FCSTD DOCUMENT  (FreeCAD 1.1R20260223 (Git shallow))
Label: wallspeakers prototype v5
License: All rights reserved
LicenseURL: http://en.wikipedia.org/wiki/All_rights_reserved
objects: TechDraw::DrawViewDimension×26, Sketcher::SketchObject×23, App::Point×12, PartDesign::Pad×11, PartDesign::Body×10, TechDraw::DrawViewAnnotation×10, PartDesign::Pocket×6, PartDesign::Hole×5, TechDraw::DrawSVGTemplate×5, TechDraw::DrawViewImage×5, TechDraw::DrawPage×5, App::DocumentObjectGroup×4, PartDesign::Revolution×3, TechDraw::DrawProjGroupItem×3, TechDraw::DrawViewDimExtent×3, PartDesign::Chamfer×3, PartDesign::Fillet×2, App::Part×2, Spreadsheet::Sheet×1, PartDesign::Thickness×1, +5 more types
note: 201 computed .brp shape members not serialized (recipe doc carries the construction recipe); baked Part::Feature solids carry a one-line shape summary decoded from their .brp

FEATURE [Spreadsheet::Sheet] Spreadsheet  label="dim"
  cells = A1='ext_width; B1(ext_width)=200; A2='ext_length; B2(ext_length)=500; A3='back_panel_width; B3(back_panel_width)==B1 - B13 * 2; C3='ext_width - rim_width * 2; A4='back_panel_length; B4(back_panel_length)==B2 - B13 * 2; C4='ext_length - rim_width * 2; A5='back_panel_radius; B5(back_panel_radius)==B11 - B13; C5='corner_roundover - rim_width; A6='back_thickness; B6(back_thickness)=5; A7='front_thickness; B7(front_thickness)=5; A8='total_depth; B8(total_depth)=48; C8='giving ourselves 2mm for wall mount fittings etc; A9='wall_thickness; B9(wall_thickness)=5; A10='front_roundover; B10(front_roundover)=10; A11='corner_roundover; B11(corner_roundover)=10; A13='rim_width; B13(rim_width)=3; A14='rim_depth; B14(rim_depth)=5.7; C14='allowing 0.7mm for a compressed 0.8mm gasket; A15='post_diameter; B15(post_diameter)=14; A17='bmr_x; B17(bmr_x)=45; C17='nudging a bit closer to the centre; A18='bmr_y; B18(bmr_y)=0; A19='bmr_screw_distance; B19(bmr_screw_distance)=24; A20='bmr_screw_offset; B20(bmr_screw_offset)=16.95; C20='bmr_screw_distance * sin(45); A21='bmr_hole_diameter; B21(bmr_hole_diameter)=41; A22='bmr_rebate_depth; B22(bmr_rebate_depth)=6; A23='bmr_post_width; B23(bmr_post_width)=7; A24='bmr_rebate_diameter; B24(bmr_rebate_diameter)=60; A26='woofer_x; B26(woofer_x)=0; A27='woofer_y; B27(woofer_y)=120; A28='woofer_support_thickness; B28(woofer_support_thickness)=7; C28='resulting in wall (5mm) + this (7mm) - rebate (8mm) = 5mm; A29='woofer_support_diameter; B29(woofer_support_diameter)=165; A30='woofer_screw_distance; B30(woofer_screw_thickness)=70.05; A31='woofer_screw_offset; B31(woofer_screw_offset)==B30 * 0.707; C31='woofer_screw_distance * sin(45); A32='woofer_hole_diameter; B32(woofer_hole_diameter)=130; A33='woofer_rebate_depth; B33(woofer_rebate_depth)=8; C33='5.3 for woofer rim, 0.7 for compressed gasket, 2 for cone resting excursion; A34='woofer_rebate_diameter; B34(woofer_rebate_diameter)=152.5; A39='woofer cutout spec; B39=127.5; C39=0.3; A40='woofer rebate spec; B40=152; C40=0.3; A41='woofer rebate depth spec; B41=5.3; C41=0.3; A43='gasket thickness (compressed); B43=0.7
FEATURE [Sketcher::SketchObject] Sketch  label="outline"
  ArcFitTolerance = 1e-06
  AttachmentSupport = -> [XY_Plane]
  ExternalTypes = [0]
  FullyConstrained = true
  MakeInternals = false
  MapMode = 5
  expr: Constraints[8] = <<dim>>.ext_width
  expr: Constraints[9] = <<dim>>.ext_length
  sketch-geometry (4):
    g0: LineSegment StartX=-100 StartY=250 StartZ=0 EndX=-100 EndY=-250 EndZ=0
    g1: LineSegment StartX=-100 StartY=-250 StartZ=0 EndX=100 EndY=-250 EndZ=0
    g2: LineSegment StartX=100 StartY=-250 StartZ=0 EndX=100 EndY=250 EndZ=0
    g3: LineSegment StartX=100 StartY=250 StartZ=0 EndX=-100 EndY=250 EndZ=0
  constraints (10):
    c: Coincident(g0,g1)
    c: Coincident(g1,g2)
    c: Coincident(g2,g3)
    c: Coincident(g3,g0)
    c: Vertical(g0)
    c: Horizontal(g1)
    c: Symmetric(g0,g2,g-2)
    c: Symmetric(g2,g1,g-1)
    c: DistanceX(g3,g3) = 200
    c: DistanceY(g2,g2) = 500
FEATURE [PartDesign::Pad] Pad  label="main solid body"
  Direction = (0,0,1)
  Length = 48
  Length2 = 10
  Profile = -> Sketch
  ReferenceAxis = -> Sketch [N_Axis]
  SideType = 0
  Suppressed = false
  Type = 0
  Type2 = 0
  expr: Length = <<dim>>.total_depth
FEATURE [Sketcher::SketchObject] Sketch002  label="woofer rebates"
  ArcFitTolerance = 1e-06
  AttachmentSupport = -> [Pad]
  ExternalTypes = [0]
  FullyConstrained = true
  MakeInternals = false
  MapMode = 5
  Placement = pos=(0,0,48) rot=(0,0,1;0rad)
  expr: Constraints[0] = <<dim>>.woofer_x
  expr: Constraints[1] = <<dim>>.woofer_y
  expr: Constraints[2] = <<dim>>.woofer_rebate_diameter
  expr: Constraints[3] = <<dim>>.woofer_rebate_diameter
  expr: Constraints[4] = <<dim>>.woofer_x
  expr: Constraints[5] = <<dim>>.woofer_y
  sketch-geometry (2):
    g0: Circle CenterX=0 CenterY=120 CenterZ=0 NormalX=0 NormalY=0 NormalZ=1 AngleXU=0 Radius=76.25
    g1: Circle CenterX=0 CenterY=-120 CenterZ=0 NormalX=0 NormalY=0 NormalZ=1 AngleXU=0 Radius=76.25
  constraints (6):
    c: DistanceX(g0,g-1) = 0
    c: DistanceY(g-1,g0) = 120
    c: Diameter(g0) = 152.5
    c: Diameter(g1) = 152.5
    c: DistanceX(g1,g-1) = 0
    c: DistanceY(g1,g-1) = 120
FEATURE [Sketcher::SketchObject] Sketch004  label="bmr rebate"
  ArcFitTolerance = 1e-06
  AttachmentSupport = -> [Pad]
  ExternalTypes = [0]
  FullyConstrained = true
  MakeInternals = false
  MapMode = 5
  Placement = pos=(0,0,48) rot=(0,0,1;0rad)
  expr: Constraints[0] = <<dim>>.bmr_rebate_diameter
  expr: Constraints[2] = <<dim>>.bmr_x
  sketch-geometry (1):
    g0: Circle CenterX=-45 CenterY=0 CenterZ=0 NormalX=0 NormalY=0 NormalZ=1 AngleXU=0 Radius=30
  constraints (3):
    c: Diameter(g0) = 60
    c: PointOnObject(g0,g-1)
    c: DistanceX(g0,g-1) = 45
FEATURE [App::Point] Origin001
  Role = Origin
FEATURE [Sketcher::SketchObject] Sketch010  label="back panel outline"
  ArcFitTolerance = 1e-06
  AttachmentSupport = -> [XY_Plane002]
  ExternalTypes = [0]
  FullyConstrained = true
  MakeInternals = false
  MapMode = 5
  expr: Constraints[17] = <<dim>>.back_panel_radius
  expr: Constraints[18] = <<dim>>.back_panel_width
  expr: Constraints[19] = <<dim>>.back_panel_length
  sketch-geometry (10):
    g0: LineSegment StartX=-97 StartY=240 StartZ=0 EndX=-97 EndY=-240 EndZ=0
    g1: LineSegment StartX=-90 StartY=-247 StartZ=0 EndX=90 EndY=-247 EndZ=0
    g2: LineSegment StartX=97 StartY=-240 StartZ=0 EndX=97 EndY=240 EndZ=0
    g3: LineSegment StartX=90 StartY=247 StartZ=0 EndX=-90 EndY=247 EndZ=0
    g4: ArcOfCircle CenterX=-90 CenterY=240 CenterZ=0 NormalX=0 NormalY=0 NormalZ=1 AngleXU=0 Radius=7 StartAngle=1.5708 EndAngle=3.14159
    g5: ArcOfCircle CenterX=-90 CenterY=-240 CenterZ=0 NormalX=0 NormalY=0 NormalZ=1 AngleXU=0 Radius=7 StartAngle=3.14159 EndAngle=4.71239
    g6: ArcOfCircle CenterX=90 CenterY=-240 CenterZ=0 NormalX=0 NormalY=0 NormalZ=1 AngleXU=0 Radius=7 StartAngle=4.71239 EndAngle=6.28319
    g7: ArcOfCircle CenterX=90 CenterY=240 CenterZ=0 NormalX=0 NormalY=0 NormalZ=1 AngleXU=0 Radius=7 StartAngle=1.3e-15 EndAngle=1.5708
    g8: GeomPoint [constr] X=-97 Y=247 Z=0
    g9: GeomPoint [constr] X=97 Y=-247 Z=0
  constraints (22):
    c: Tangent(g0,g4) = -1.5708
    c: Tangent(g0,g5) = -1.5708
    c: Tangent(g1,g5) = -1.5708
    c: Tangent(g1,g6) = -1.5708
    c: Tangent(g2,g6) = -1.5708
    c: Tangent(g2,g7) = -1.5708
    c: Tangent(g3,g7) = -1.5708
    c: Tangent(g3,g4) = -1.5708
    c: Vertical(g0)
    c: Vertical(g2)
    c: Horizontal(g1)
    c: Horizontal(g3)
    c: Equal(g5,g6)
    c: PointOnObject(g8,g0)
    c: PointOnObject(g8,g3)
    c: PointOnObject(g9,g1)
    c: PointOnObject(g9,g2)
    c: Radius(g5) = 7
    c: DistanceX(g0,g2) = 194
    c: DistanceY(g1,g3) = 494
    c: Symmetric(g0,g2,g-2)
    c: Symmetric(g3,g1,g-1)
FEATURE [PartDesign::Pad] Pad004  label="back panel pad"
  Direction = (0,0,1)
  Length = 5
  Length2 = 10
  Profile = -> Sketch010
  ReferenceAxis = -> Sketch010 [N_Axis]
  SideType = 0
  Suppressed = false
  Type = 0
  Type2 = 0
  expr: Length = <<dim>>.back_thickness
FEATURE [App::Point] Origin005
  Role = Origin
FEATURE [App::Point] Origin007
  Role = Origin
FEATURE [Sketcher::SketchObject] Sketch015  label="frame outline"
  ArcFitTolerance = 1e-06
  ExternalTypes = [0]
  FullyConstrained = true
  MakeInternals = false
  MapMode = 53
  sketch-geometry (8):
    g0: ArcOfCircle CenterX=0 CenterY=0 CenterZ=0 NormalX=0 NormalY=0 NormalZ=1 AngleXU=0 Radius=20.5 StartAngle=1.5708 EndAngle=3.14159
    g1: ArcOfCircle CenterX=0 CenterY=0 CenterZ=0 NormalX=0 NormalY=0 NormalZ=1 AngleXU=0 Radius=23.25 StartAngle=2.58919 EndAngle=3.14159
    g2: ArcOfCircle CenterX=-16.8247 CenterY=16.8336 CenterZ=0 NormalX=0 NormalY=0 NormalZ=1 AngleXU=0 Radius=3.72 StartAngle=0.960084 EndAngle=3.75505
    g3: ArcOfCircle CenterX=-21.785 CenterY=13.3876 CenterZ=0 NormalX=0 NormalY=0 NormalZ=1 AngleXU=0 Radius=2.32 StartAngle=5.74581 EndAngle=6.88028
    g4: ArcOfCircle CenterX=-13.3758 CenterY=21.792 CenterZ=0 NormalX=0 NormalY=0 NormalZ=1 AngleXU=0 Radius=2.32 StartAngle=4.10939 EndAngle=5.24385
    g5: LineSegment StartX=1.4e-15 StartY=20.5 StartZ=0 EndX=1.4e-15 EndY=23.25 EndZ=0
    g6: LineSegment StartX=-20.5 StartY=2.8e-15 StartZ=0 EndX=-23.25 EndY=2.8e-15 EndZ=0
    g7: ArcOfCircle CenterX=0 CenterY=0 CenterZ=0 NormalX=0 NormalY=0 NormalZ=1 AngleXU=0 Radius=23.25 StartAngle=1.5708 EndAngle=2.1232
  constraints (28):
    c: Coincident(g0,g-1)
    c: PointOnObject(g1,g-1)
    c: PointOnObject(g1,g-2)
    c: DistanceX(g7,g-1) = 12.2
    c: DistanceY(g-1,g1) = 12.2
    c: Radius(g2) = 3.72
    c: Coincident(g3,g2)
    c: Coincident(g3,g1)
    c: Coincident(g4,g7)
    c: Coincident(g4,g2)
    c: Radius(g3) = 2.32
    c: Radius(g4) = 2.32
    c: Angle(g3) = 1.13446
    c: Angle(g4) = 1.13446
    c: Distance(g2,g-1) = 23.8
    c: Angle(g2) = 2.79497
    c: Vertical(g5)
    c: PointOnObject(g5,g-2)
    c: Horizontal(g6)
    c: PointOnObject(g6,g-1)
    c: Diameter(g0) = 41
    c: Coincident(g5,g0)
    c: Coincident(g6,g0)
    c: Diameter(g1) = 46.5
    c: Coincident(g5,g7)
    c: Coincident(g6,g1)
    c: Coincident(g1,g7)
    c: Radius(g7) = 23.25
FEATURE [App::Point] Origin009
  Role = Origin
FEATURE [Sketcher::SketchObject] Sketch017  label="Woofer gasket"
  ArcFitTolerance = 1e-06
  AttachmentSupport = -> [Origin008]
  ExternalTypes = [0]
  FullyConstrained = true
  MakeInternals = false
  MapMode = 5
  expr: Constraints[0] = <<dim>>.woofer_rebate_diameter - 0.5
  expr: Constraints[11] = <<dim>>.woofer_screw_offset
  expr: Constraints[12] = <<dim>>.woofer_screw_offset
  expr: Constraints[1] = <<dim>>.woofer_hole_diameter + 2
  sketch-geometry (6):
    g0: Circle CenterX=0 CenterY=0 CenterZ=0 NormalX=0 NormalY=0 NormalZ=1 AngleXU=0 Radius=76
    g1: Circle CenterX=0 CenterY=0 CenterZ=0 NormalX=0 NormalY=0 NormalZ=1 AngleXU=0 Radius=66
    g2: Circle CenterX=49.5253 CenterY=-49.5253 CenterZ=0 NormalX=0 NormalY=0 NormalZ=1 AngleXU=0 Radius=2.125
    g3: Circle CenterX=49.5253 CenterY=49.5253 CenterZ=0 NormalX=0 NormalY=0 NormalZ=1 AngleXU=0 Radius=2.125
    g4: Circle CenterX=-49.5253 CenterY=49.5253 CenterZ=0 NormalX=0 NormalY=0 NormalZ=1 AngleXU=0 Radius=2.125
    g5: Circle CenterX=-49.5253 CenterY=-49.5253 CenterZ=0 NormalX=0 NormalY=0 NormalZ=1 AngleXU=0 Radius=2.125
  constraints (13):
    c: Diameter(g0) = 152
    c: Diameter(g1) = 132
    c: Coincident(g0,g1)
    c: Coincident(g-1,g0)
    c: Equal(g2,g3)
    c: Equal(g2,g4)
    c: Equal(g2,g5)
    c: Diameter(g2) = 4.25
    c: Symmetric(g4,g3,g-2)
    c: Symmetric(g5,g2,g-2)
    c: Symmetric(g4,g5,g-1)
    c: DistanceX(g-1,g3) = 49.5253
    c: DistanceY(g-1,g3) = 49.5253
FEATURE [Sketcher::SketchObject] Sketch018  label="screw posts sketch"
  ArcFitTolerance = 1e-06
  AttachmentOffset = pos=(0,0,-5.7) rot=(0,0,1;0rad)
  AttachmentSupport = -> [Pad]
  ExternalTypes = [0]
  FullyConstrained = true
  MakeInternals = false
  MapMode = 5
  Placement = pos=(0,0,5.7) rot=(1,0,0;3.14159rad)
  expr: .AttachmentOffset.Base.z = -<<dim>>.rim_depth
  expr: Constraints[0] = <<dim>>.ext_length / 2 - <<dim>>.post_diameter / 2 - 2
  expr: Constraints[1] = <<dim>>.ext_width / 2 - <<dim>>.post_diameter / 2 - 2
  expr: Constraints[4] = <<dim>>.ext_width / 2 - <<dim>>.post_diameter / 2 - 2
  sketch-geometry (9):
    g0: Circle CenterX=-91 CenterY=241 CenterZ=0 NormalX=0 NormalY=0 NormalZ=1 AngleXU=0 Radius=2
    g1: Circle CenterX=91 CenterY=241 CenterZ=0 NormalX=0 NormalY=0 NormalZ=1 AngleXU=0 Radius=2
    g2: Circle CenterX=-91 CenterY=67.5 CenterZ=0 NormalX=0 NormalY=0 NormalZ=1 AngleXU=0 Radius=2
    g3: Circle CenterX=12.5 CenterY=0 CenterZ=0 NormalX=0 NormalY=0 NormalZ=1 AngleXU=0 Radius=2
    g4: Circle CenterX=-91 CenterY=-67.5 CenterZ=0 NormalX=0 NormalY=0 NormalZ=1 AngleXU=0 Radius=2
    g5: Circle CenterX=91 CenterY=67.5 CenterZ=0 NormalX=0 NormalY=0 NormalZ=1 AngleXU=0 Radius=2
    g6: Circle CenterX=91 CenterY=-67.5 CenterZ=0 NormalX=0 NormalY=0 NormalZ=1 AngleXU=0 Radius=2
    g7: Circle CenterX=-91 CenterY=-241 CenterZ=0 NormalX=0 NormalY=0 NormalZ=1 AngleXU=0 Radius=2
    g8: Circle CenterX=91 CenterY=-241 CenterZ=0 NormalX=0 NormalY=0 NormalZ=1 AngleXU=0 Radius=2
  constraints (14):
    c: DistanceY(g-1,g0) = 241
    c: DistanceX(g0,g-1) = 91
    c: Symmetric(g0,g1,g-2)
    c: DistanceY(g-1,g2) = 67.5
    c: DistanceX(g2,g-1) = 91
    c: DistanceX(g-1,g3) = 12.5
    c: PointOnObject(g3,g-1)
    c: Symmetric(g2,g4,g-1)
    c: Symmetric(g2,g5,g-2)
    c: Symmetric(g5,g6,g-1)
    c: Symmetric(g1,g8,g-1)
    c: Symmetric(g0,g7,g-1)
    c: Equal(g0, g1-g8) x8
    c: Diameter(g0) = 4
FEATURE [App::Point] Origin011
  Role = Origin
FEATURE [Sketcher::SketchObject] Sketch019
  ArcFitTolerance = 1e-06
  AttachmentSupport = -> [Origin010]
  ExternalTypes = [0]
  FullyConstrained = true
  MakeInternals = false
  MapMode = 5
  Placement = pos=(0,0,0) rot=(0.57735,0.57735,0.57735;2.0944rad)
  sketch-geometry (6):
    g0: LineSegment StartX=0 StartY=32 StartZ=0 EndX=-76 EndY=32 EndZ=0
    g1: LineSegment StartX=-76 StartY=32 StartZ=0 EndX=-76 EndY=26.7 EndZ=0
    g2: LineSegment StartX=-76 StartY=26.7 StartZ=0 EndX=-63.75 EndY=26.7 EndZ=0
    g3: LineSegment StartX=-63.75 StartY=26.7 StartZ=0 EndX=-55 EndY=6e-16 EndZ=0
    g4: LineSegment StartX=-55 StartY=6e-16 StartZ=0 EndX=0 EndY=6e-16 EndZ=0
    g5: LineSegment StartX=0 StartY=6e-16 StartZ=0 EndX=0 EndY=32 EndZ=0
  constraints (17):
    c: PointOnObject(g0,g-2)
    c: Horizontal(g0)
    c: Coincident(g0,g1)
    c: Vertical(g1)
    c: Coincident(g1,g2)
    c: Horizontal(g2)
    c: Coincident(g2,g3)
    c: Coincident(g3,g4)
    c: Horizontal(g4)
    c: Coincident(g4,g5)
    c: Coincident(g5,g0)
    c: DistanceX(g0,g0) = 76
    c: DistanceY(g1,g1) = 5.3
    c: DistanceX(g2,g-1) = 63.75
    c: DistanceX(g3,g-1) = 55
    c: DistanceY(g5,g5) = 32
    c: Coincident(g4,g-1)
FEATURE [PartDesign::Revolution] Revolution
  Angle = 360
  Angle2 = 60
  Axis = (0,0,1)
  Base = (0,0,0)
  FuseOrder = 0
  Profile = -> Sketch019
  ReferenceAxis = -> Sketch019 [V_Axis]
  Suppressed = false
  Type = 0
FEATURE [PartDesign::Body] Body005  label="woofer rough model for fitting"
  AllowCompound = false
  Group = -> [Sketch019,Revolution]
  Origin = -> Origin010
  Placement = pos=(0,120,15) rot=(0,0,1;0rad)
  Tip = -> Revolution
FEATURE [PartDesign::Pad] Pad010  label="woofer gasket pad"
  Direction = (0,0,1)
  Length = 0.7
  Length2 = 10
  Profile = -> Sketch017
  ReferenceAxis = -> Sketch017 [N_Axis]
  SideType = 0
  Suppressed = false
  Type = 0
  Type2 = 0
FEATURE [PartDesign::Body] Body004  label="woofer gasket"
  AllowCompound = false
  Group = -> [Sketch017,Pad010]
  Origin = -> Origin008
  Placement = pos=(0,120,40) rot=(0,0,1;0rad)
  Tip = -> Pad010
  expr: .Placement.Base.y = <<dim>>.woofer_y
  expr: .Placement.Base.z = <<dim>>.total_depth - <<dim>>.woofer_rebate_depth
FEATURE [App::Point] Origin015
  Role = Origin
FEATURE [Sketcher::SketchObject] Sketch020
  ArcFitTolerance = 1e-06
  AttachmentSupport = -> [Origin014]
  ExternalTypes = [0]
  FullyConstrained = true
  MakeInternals = false
  MapMode = 5
  sketch-geometry (6):
    g0: Circle CenterX=0 CenterY=0 CenterZ=0 NormalX=0 NormalY=0 NormalZ=1 AngleXU=0 Radius=30
    g1: Circle CenterX=0 CenterY=0 CenterZ=0 NormalX=0 NormalY=0 NormalZ=1 AngleXU=0 Radius=20.75
    g2: Circle CenterX=16.95 CenterY=-16.95 CenterZ=0 NormalX=0 NormalY=0 NormalZ=1 AngleXU=0 Radius=1.75
    g3: Circle CenterX=16.95 CenterY=16.95 CenterZ=0 NormalX=0 NormalY=0 NormalZ=1 AngleXU=0 Radius=1.75
    g4: Circle CenterX=-16.95 CenterY=16.95 CenterZ=0 NormalX=0 NormalY=0 NormalZ=1 AngleXU=0 Radius=1.75
    g5: Circle CenterX=-16.95 CenterY=-16.95 CenterZ=0 NormalX=0 NormalY=0 NormalZ=1 AngleXU=0 Radius=1.75
  constraints (13):
    c: Diameter(g0) = 60
    c: Diameter(g1) = 41.5
    c: Coincident(g0,g1)
    c: Coincident(g-1,g0)
    c: Equal(g2,g3)
    c: Equal(g2,g4)
    c: Equal(g2,g5)
    c: Diameter(g2) = 3.5
    c: Symmetric(g4,g3,g-2)
    c: Symmetric(g5,g2,g-2)
    c: Symmetric(g4,g5,g-1)
    c: DistanceX(g-1,g3) = 16.95
    c: DistanceY(g-1,g3) = 16.95
FEATURE [PartDesign::Pad] Pad011
  Direction = (0,0,1)
  Length = 0.7
  Length2 = 10
  Profile = -> Sketch020
  ReferenceAxis = -> Sketch020 [N_Axis]
  SideType = 0
  Suppressed = false
  Type = 0
  Type2 = 0
FEATURE [PartDesign::Body] Body007  label="bmr gasket"
  AllowCompound = false
  Group = -> [Sketch020,Pad011]
  Origin = -> Origin014
  Placement = pos=(-45,0,42) rot=(0,0,1;0rad)
  Tip = -> Pad011
  expr: .Placement.Base.x = -<<dim>>.bmr_x
  expr: .Placement.Base.z = <<dim>>.total_depth - <<dim>>.bmr_rebate_depth
FEATURE [Sketcher::SketchObject] Sketch021  label="rim sketch"
  ArcFitTolerance = 1e-06
  AttachmentSupport = -> [Pad]
  ExternalTypes = [0]
  FullyConstrained = true
  MakeInternals = false
  MapMode = 5
  Placement = pos=(0,0,0) rot=(1,0,0;3.14159rad)
  expr: Constraints[18] = <<dim>>.ext_width - <<dim>>.rim_width * 2
  expr: Constraints[19] = <<dim>>.ext_length - <<dim>>.rim_width * 2
  sketch-geometry (10):
    g0: LineSegment StartX=-97 StartY=239.5 StartZ=0 EndX=-97 EndY=-239.5 EndZ=0
    g1: LineSegment StartX=-89.5 StartY=-247 StartZ=0 EndX=89.5 EndY=-247 EndZ=0
    g2: LineSegment StartX=97 StartY=-239.5 StartZ=0 EndX=97 EndY=239.5 EndZ=0
    g3: LineSegment StartX=89.5 StartY=247 StartZ=0 EndX=-89.5 EndY=247 EndZ=0
    g4: ArcOfCircle CenterX=-89.5 CenterY=239.5 CenterZ=0 NormalX=0 NormalY=0 NormalZ=1 AngleXU=0 Radius=7.5 StartAngle=1.5708 EndAngle=3.14159
    g5: ArcOfCircle CenterX=-89.5 CenterY=-239.5 CenterZ=0 NormalX=0 NormalY=0 NormalZ=1 AngleXU=0 Radius=7.5 StartAngle=3.14159 EndAngle=4.71239
    g6: ArcOfCircle CenterX=89.5 CenterY=-239.5 CenterZ=0 NormalX=0 NormalY=0 NormalZ=1 AngleXU=0 Radius=7.5 StartAngle=4.71239 EndAngle=6.28319
    g7: ArcOfCircle CenterX=89.5 CenterY=239.5 CenterZ=0 NormalX=0 NormalY=0 NormalZ=1 AngleXU=0 Radius=7.5 StartAngle=0 EndAngle=1.5708
    g8: GeomPoint [constr] X=-97 Y=247 Z=0
    g9: GeomPoint [constr] X=97 Y=-247 Z=0
  constraints (22):
    c: Tangent(g0,g4) = -1.5708
    c: Tangent(g0,g5) = -1.5708
    c: Tangent(g1,g5) = -1.5708
    c: Tangent(g1,g6) = -1.5708
    c: Tangent(g2,g6) = -1.5708
    c: Tangent(g2,g7) = -1.5708
    c: Tangent(g3,g7) = -1.5708
    c: Tangent(g3,g4) = -1.5708
    c: Vertical(g0)
    c: Vertical(g2)
    c: Horizontal(g1)
    c: Horizontal(g3)
    c: Equal(g5,g6)
    c: PointOnObject(g8,g0)
    c: PointOnObject(g8,g3)
    c: PointOnObject(g9,g1)
    c: PointOnObject(g9,g2)
    c: Radius(g5) = 7.5
    c: DistanceX(g0,g2) = 194
    c: DistanceY(g1,g3) = 494
    c: Symmetric(g0,g2,g-2)
    c: Symmetric(g3,g1,g-1)
FEATURE [Sketcher::SketchObject] Sketch024  label="cable entry hole sketch"
  ArcFitTolerance = 1e-06
  ExternalTypes = [0]
  FullyConstrained = true
  MakeInternals = false
  MapMode = 5
  Placement = pos=(0,0,0) rot=(1,0,0;3.14159rad)
  sketch-geometry (4):
    g0: LineSegment StartX=-3.5 StartY=8.015 StartZ=0 EndX=-3.5 EndY=-8.015 EndZ=0
    g1: LineSegment StartX=-3.5 StartY=-8.015 StartZ=0 EndX=3.5 EndY=-8.015 EndZ=0
    g2: LineSegment StartX=3.5 StartY=-8.015 StartZ=0 EndX=3.5 EndY=8.015 EndZ=0
    g3: LineSegment StartX=3.5 StartY=8.015 StartZ=0 EndX=-3.5 EndY=8.015 EndZ=0
  constraints (10):
    c: Coincident(g0,g1)
    c: Coincident(g1,g2)
    c: Coincident(g2,g3)
    c: Coincident(g3,g0)
    c: Vertical(g0)
    c: Horizontal(g1)
    c: DistanceY(g0,g0) = 16.03
    c: DistanceX(g3,g3) = 7
    c: Symmetric(g0,g2,g-2)
    c: Symmetric(g2,g1,g-1)
FEATURE [PartDesign::Pocket] Pocket004  label="cable entry hole"
  BaseFeature = -> Pad004
  Direction = (0,1e-16,1)
  Length = 5
  Length2 = 5
  Profile = -> Sketch024
  ReferenceAxis = -> Sketch024 [N_Axis]
  SideType = 0
  Suppressed = false
  Type = 0
  Type2 = 0
FEATURE [Sketcher::SketchObject] Sketch027  label="base shape"
  ArcFitTolerance = 1e-06
  ExternalTypes = [0]
  FullyConstrained = true
  MakeInternals = false
  MapMode = 53
  expr: Constraints[7] = <<dim>>.bmr_rebate_diameter - 0.1
  sketch-geometry (4):
    g0: ArcOfCircle CenterX=0 CenterY=0 CenterZ=0 NormalX=0 NormalY=0 NormalZ=1 AngleXU=0 Radius=29.95 StartAngle=1.5708 EndAngle=3.14159
    g1: LineSegment StartX=1.4e-15 StartY=29.95 StartZ=0 EndX=1.4e-15 EndY=23.1 EndZ=0
    g2: LineSegment StartX=-29.95 StartY=2.8e-15 StartZ=0 EndX=-23.1 EndY=2.8e-15 EndZ=0
    g3: ArcOfCircle CenterX=0 CenterY=0 CenterZ=0 NormalX=0 NormalY=0 NormalZ=1 AngleXU=0 Radius=23.1 StartAngle=1.5708 EndAngle=3.14159
  constraints (13):
    c: Coincident(g0,g-1)
    c: PointOnObject(g3,g-1)
    c: PointOnObject(g3,g-2)
    c: Vertical(g1)
    c: PointOnObject(g1,g-2)
    c: Horizontal(g2)
    c: PointOnObject(g2,g-1)
    c: Diameter(g0) = 59.9
    c: Coincident(g1,g0)
    c: Coincident(g2,g0)
    c: Coincident(g1,g3)
    c: Radius(g3) = 23.1
    c: Coincident(g3,g2)
FEATURE [App::Point] Origin019
  Role = Origin
FEATURE [Sketcher::SketchObject] Sketch030
  ArcFitTolerance = 1e-06
  AttachmentOffset = pos=(-52,6.35,3) rot=(0,0,1;0rad)
  AttachmentSupport = -> [Origin018]
  ExternalTypes = [0]
  FullyConstrained = true
  MakeInternals = false
  MapMode = 5
  Placement = pos=(-52,-3,6.35) rot=(1,0,0;1.5708rad)
  sketch-geometry (10):
    g0: LineSegment StartX=0 StartY=0 StartZ=0 EndX=20 EndY=-3.2e-14 EndZ=0
    g1: LineSegment StartX=0 StartY=0 StartZ=0 EndX=0 EndY=15 EndZ=0
    g2: ArcOfCircle CenterX=0 CenterY=-14.2 CenterZ=0 NormalX=0 NormalY=0 NormalZ=1 AngleXU=0 Radius=24.5284 StartAngle=0.617406 EndAngle=1.40699
    g3-g6: Circle [constr] x4 (B-spline internal-alignment scaffolding for g7; pole/knot coordinates omitted)
    g7: BSplineCurve PolesCount=4 KnotsCount=2 Degree=3 IsPeriodic=0
    g8: GeomPoint [constr] X=4 Y=10 Z=0
    g9: GeomPoint [constr] X=0 Y=15 Z=0
  constraints (23):
    c: Coincident(g0,g-1)
    c: PointOnObject(g0,g-1)
    c: Coincident(g1,g0)
    c: PointOnObject(g1,g-2)
    c: DistanceY(g1,g1) = 15
    c: DistanceX(g0,g0) = 20
    c: Coincident(g2,g0)
    c: PointOnObject(g2,g-2)
    c: Distance(g2,g-2) = 4
    c: DistanceY(g-1,g2) = 10
    c: Weight(g3) = 1
    c: Equal(g3,g4)
    c: Equal(g3,g5)
    c: Equal(g3,g6)
    c: InternalAlignment(g3-g6 -> g7) x4
    c: InternalAlignment(g8,g7)
    c: InternalAlignment(g9,g7)
    c: Coincident(g3,g2)
    c: Coincident(g6,g1)
    c: DistanceY(g-1,g5) = 14
    c: DistanceX(g-1,g5) = 0.85
    c: DistanceY(g-1,g4) = 10.9
    c: DistanceX(g-1,g4) = 1.5
FEATURE [PartDesign::Revolution] Revolution001
  Angle = 360
  Angle2 = 60
  Axis = (0,2e-16,1)
  Base = (-52,-3,6.35)
  FuseOrder = 0
  Profile = -> Sketch030
  ReferenceAxis = -> Sketch030 [V_Axis]
  Reversed = true
  Suppressed = false
  Type = 0
FEATURE [PartDesign::Body] Body008  label="BMR backwave diffuser"
  AllowCompound = false
  Group = -> [Sketch030,Revolution001]
  Origin = -> Origin018
  Tip = -> Revolution001
FEATURE [PartDesign::Thickness] Thickness001  label="thickness main body"
  Base = -> Pad [Face5]
  BaseFeature = -> Pad
  Intersection = false
  Join = 0
  Mode = 0
  Reversed = true
  SupportTransform = false
  Suppressed = false
  Value = 5
FEATURE [Sketcher::SketchObject] Sketch001  label="driver holes"
  ArcFitTolerance = 1e-06
  AttachmentSupport = -> [Thickness001]
  ExternalTypes = [0]
  FullyConstrained = true
  MakeInternals = false
  MapMode = 5
  Placement = pos=(0,0,48) rot=(0,0,1;0rad)
  expr: Constraints[0] = <<dim>>.bmr_hole_diameter
  expr: Constraints[2] = <<dim>>.bmr_x
  expr: Constraints[3] = <<dim>>.woofer_x
  expr: Constraints[4] = <<dim>>.woofer_y
  expr: Constraints[5] = <<dim>>.woofer_hole_diameter
  expr: Constraints[6] = <<dim>>.woofer_hole_diameter
  expr: Constraints[7] = <<dim>>.woofer_x
  expr: Constraints[8] = <<dim>>.woofer_y
  sketch-geometry (3):
    g0: Circle CenterX=-45 CenterY=0 CenterZ=0 NormalX=0 NormalY=0 NormalZ=1 AngleXU=0 Radius=20.5
    g1: Circle CenterX=0 CenterY=120 CenterZ=0 NormalX=0 NormalY=0 NormalZ=1 AngleXU=0 Radius=65
    g2: Circle CenterX=0 CenterY=-120 CenterZ=0 NormalX=0 NormalY=0 NormalZ=1 AngleXU=0 Radius=65
  constraints (9):
    c: Diameter(g0) = 41
    c: PointOnObject(g0,g-1)
    c: DistanceX(g0,g-1) = 45
    c: DistanceX(g1,g-1) = 0
    c: DistanceY(g-1,g1) = 120
    c: Diameter(g1) = 130
    c: Diameter(g2) = 130
    c: DistanceX(g2,g-1) = 0
    c: DistanceY(g2,g-1) = 120
FEATURE [Sketcher::SketchObject] Sketch003  label="woofer support rings"
  ArcFitTolerance = 1e-06
  AttachmentSupport = -> [Thickness001]
  ExternalTypes = [0]
  FullyConstrained = true
  MakeInternals = false
  MapMode = 5
  Placement = pos=(0,0,43) rot=(1,0,0;3.14159rad)
  expr: Constraints[0] = <<dim>>.woofer_x
  expr: Constraints[11] = <<dim>>.woofer_y
  expr: Constraints[1] = <<dim>>.woofer_y
  expr: Constraints[2] = <<dim>>.woofer_hole_diameter
  expr: Constraints[3] = <<dim>>.woofer_hole_diameter
  expr: Constraints[4] = <<dim>>.woofer_x
  expr: Constraints[5] = <<dim>>.woofer_y
  expr: Constraints[7] = <<dim>>.woofer_y
  expr: Constraints[8] = <<dim>>.woofer_support_diameter
  expr: Constraints[9] = <<dim>>.woofer_support_diameter
  sketch-geometry (4):
    g0: Circle CenterX=0 CenterY=120 CenterZ=0 NormalX=0 NormalY=0 NormalZ=1 AngleXU=0 Radius=65
    g1: Circle CenterX=0 CenterY=-120 CenterZ=0 NormalX=0 NormalY=0 NormalZ=1 AngleXU=0 Radius=65
    g2: Circle CenterX=0 CenterY=120 CenterZ=0 NormalX=0 NormalY=0 NormalZ=1 AngleXU=0 Radius=82.5
    g3: Circle CenterX=0 CenterY=-120 CenterZ=0 NormalX=0 NormalY=0 NormalZ=1 AngleXU=0 Radius=82.5
  constraints (12):
    c: DistanceX(g0,g-1) = 0
    c: DistanceY(g-1,g0) = 120
    c: Diameter(g0) = 130
    c: Diameter(g1) = 130
    c: DistanceX(g1,g-1) = 0
    c: DistanceY(g1,g-1) = 120
    c: DistanceX(g2,g-1) = 0
    c: DistanceY(g-1,g2) = 120
    c: Diameter(g2) = 165
    c: Diameter(g3) = 165
    c: DistanceX(g3,g-1) = 0
    c: DistanceY(g3,g-1) = 120
FEATURE [Sketcher::SketchObject] Sketch008  label="bmr support ring"
  ArcFitTolerance = 1e-06
  AttachmentSupport = -> [Thickness001]
  ExternalTypes = [0]
  FullyConstrained = true
  MakeInternals = true
  MapMode = 5
  Placement = pos=(0,0,43) rot=(1,0,0;3.14159rad)
  expr: Constraints[0] = <<dim>>.bmr_rebate_diameter + 15
  expr: Constraints[2] = <<dim>>.bmr_x
  expr: Constraints[3] = <<dim>>.bmr_hole_diameter
  expr: Constraints[5] = <<dim>>.bmr_x
  sketch-geometry (2):
    g0: Circle CenterX=-45 CenterY=0 CenterZ=0 NormalX=0 NormalY=0 NormalZ=1 AngleXU=0 Radius=37.5
    g1: Circle CenterX=-45 CenterY=0 CenterZ=0 NormalX=0 NormalY=0 NormalZ=1 AngleXU=0 Radius=20.5
  constraints (6):
    c: Diameter(g0) = 75
    c: PointOnObject(g0,g-1)
    c: DistanceX(g0,g-1) = 45
    c: Diameter(g1) = 41
    c: PointOnObject(g1,g-1)
    c: DistanceX(g1,g-1) = 45
FEATURE [Sketcher::SketchObject] Sketch031  label="internal baffle sketch"
  ArcFitTolerance = 1e-06
  AttachmentSupport = -> [Thickness001]
  ExternalTypes = [0]
  FullyConstrained = true
  MakeInternals = false
  MapMode = 5
  Placement = pos=(0,0,43) rot=(1,0,0;3.14159rad)
  sketch-geometry (12):
    g0: LineSegment StartX=15 StartY=30 StartZ=0 EndX=15 EndY=-30 EndZ=0
    g1: LineSegment StartX=15 StartY=-30 StartZ=0 EndX=-90 EndY=-70 EndZ=0
    g2: LineSegment StartX=-90 StartY=-70 StartZ=0 EndX=-95 EndY=-70 EndZ=0
    g3: LineSegment StartX=15 StartY=30 StartZ=0 EndX=-90 EndY=70 EndZ=0
    g4: LineSegment StartX=-90 StartY=70 StartZ=0 EndX=-95 EndY=70 EndZ=0
    g5: LineSegment StartX=-95 StartY=-70 StartZ=0 EndX=-95 EndY=-65 EndZ=0
    g6: LineSegment StartX=-95 StartY=-65 StartZ=0 EndX=-90 EndY=-65 EndZ=0
    g7: LineSegment StartX=-90 StartY=-65 StartZ=0 EndX=10 EndY=-26.9048 EndZ=0
    g8: LineSegment StartX=10 StartY=-26.9048 StartZ=0 EndX=10 EndY=26.9048 EndZ=0
    g9: LineSegment StartX=10 StartY=26.9048 StartZ=0 EndX=-90 EndY=65 EndZ=0
    g10: LineSegment StartX=-90 StartY=65 StartZ=0 EndX=-95 EndY=65 EndZ=0
    g11: LineSegment StartX=-95 StartY=65 StartZ=0 EndX=-95 EndY=70 EndZ=0
  constraints (31):
    c: Parallel(g9,g3)
    c: Parallel(g7,g1)
    c: Parallel(g6,g2)
    c: Parallel(g4,g10)
    c: Coincident(g8,g9)
    c: Coincident(g8,g7)
    c: Coincident(g1,g0)
    c: Coincident(g0,g3)
    c: Coincident(g6,g5)
    c: Coincident(g5,g2)
    c: Coincident(g2,g1)
    c: Coincident(g7,g6)
    c: Coincident(g4,g3)
    c: Coincident(g9,g10)
    c: Coincident(g11,g10)
    c: Coincident(g4,g11)
    c: Symmetric(g0,g0,g-1)
    c: Symmetric(g8,g7,g-1)
    c: DistanceY(g11,g11) = 5
    c: Symmetric(g10,g5,g-1)
    c: Symmetric(g4,g2,g-1)
    c: Symmetric(g9,g6,g-1)
    c: Horizontal(g4)
    c: Distance(g9,g3) = 5
    c: DistanceX(g-1,g8) = 10
    c: DistanceX(g4,g4) = 5
    c: DistanceX(g8,g0) = 5
    c: DistanceX(g4,g-1) = 95
    c: DistanceY(g-1,g4) = 70
    c: Vertical(g5)
    c: DistanceY(g-1,g0) = 30
FEATURE [Sketcher::SketchObject] Sketch032  label="cc of screw posts sketch"
  ArcFitTolerance = 1e-06
  AttachmentSupport = -> [Pad004]
  ExternalTypes = [0]
  FullyConstrained = true
  MakeInternals = false
  MapMode = 5
  Placement = pos=(0,0,0) rot=(1,0,0;3.14159rad)
  expr: Constraints[0] = Sketch018.Constraints[0]
  expr: Constraints[1] = Sketch018.Constraints[1]
  expr: Constraints[20] = Sketch018.Constraints[20]
  expr: Constraints[3] = Sketch018.Constraints[3]
  expr: Constraints[4] = Sketch018.Constraints[4]
  expr: Constraints[5] = Sketch018.Constraints[5]
  sketch-geometry (9):
    g0: Circle CenterX=-91 CenterY=241 CenterZ=0 NormalX=0 NormalY=0 NormalZ=1 AngleXU=0 Radius=2
    g1: Circle CenterX=91 CenterY=241 CenterZ=0 NormalX=0 NormalY=0 NormalZ=1 AngleXU=0 Radius=2
    g2: Circle CenterX=-91 CenterY=67.5 CenterZ=0 NormalX=0 NormalY=0 NormalZ=1 AngleXU=0 Radius=2
    g3: Circle CenterX=12.5 CenterY=0 CenterZ=0 NormalX=0 NormalY=0 NormalZ=1 AngleXU=0 Radius=2
    g4: Circle CenterX=-91 CenterY=-67.5 CenterZ=0 NormalX=0 NormalY=0 NormalZ=1 AngleXU=0 Radius=2
    g5: Circle CenterX=91 CenterY=67.5 CenterZ=0 NormalX=0 NormalY=0 NormalZ=1 AngleXU=0 Radius=2
    g6: Circle CenterX=91 CenterY=-67.5 CenterZ=0 NormalX=0 NormalY=0 NormalZ=1 AngleXU=0 Radius=2
    g7: Circle CenterX=-91 CenterY=-241 CenterZ=0 NormalX=0 NormalY=0 NormalZ=1 AngleXU=0 Radius=2
    g8: Circle CenterX=91 CenterY=-241 CenterZ=0 NormalX=0 NormalY=0 NormalZ=1 AngleXU=0 Radius=2
  constraints (14):
    c: DistanceY(g-1,g0) = 241
    c: DistanceX(g0,g-1) = 91
    c: Symmetric(g0,g1,g-2)
    c: DistanceY(g-1,g2) = 67.5
    c: DistanceX(g2,g-1) = 91
    c: DistanceX(g-1,g3) = 12.5
    c: PointOnObject(g3,g-1)
    c: Symmetric(g2,g4,g-1)
    c: Symmetric(g2,g5,g-2)
    c: Symmetric(g5,g6,g-1)
    c: Symmetric(g1,g8,g-1)
    c: Symmetric(g0,g7,g-1)
    c: Equal(g0, g1-g8) x8
    c: Diameter(g0) = 4
FEATURE [PartDesign::Hole] Hole008  label="back panel screw pass-throughs"
  BaseFeature = -> Pocket004
  BaseProfileType = 7
  CustomThreadClearance = 0
  Depth = 5
  DepthType = 0
  Diameter = 4.5
  DrillForDepth = false
  DrillPoint = 1
  DrillPointAngle = 118
  HoleCutCountersinkAngle = 90
  HoleCutCustomValues = false
  HoleCutDepth = 4.5
  HoleCutDiameter = 9
  HoleCutType = 2
  ModelThread = false
  Profile = -> Sketch032
  Suppressed = false
  Tapered = false
  TaperedAngle = 90
  ThreadClass = 0
  ThreadDepth = 5
  ThreadDepthType = 0
  ThreadDiameter = 4
  ThreadDirection = 0
  ThreadFit = 0
  ThreadSize = 11
  ThreadType = 1
  Threaded = false
  UseCustomThreadClearance = false
  expr: Depth = <<dim>>.back_thickness
FEATURE [PartDesign::Body] Body002  label="back panel"
  AllowCompound = false
  Group = -> [Sketch010,Pad004,Sketch032,Sketch024,Pocket004,Hole008]
  Origin = -> Origin004
  Tip = -> Hole008
FEATURE [PartDesign::Fillet] Fillet006  label="Interior fillets"
  Base = -> Thickness001 [Edge18,Edge24,Edge22,Edge20]
  BaseFeature = -> Thickness001
  Radius = 5
  SupportTransform = false
  Suppressed = false
  UseAllEdges = false
  expr: Radius = <<dim>>.front_roundover - <<dim>>.wall_thickness
FEATURE [PartDesign::Pad] Pad017  label="screw posts pad"
  BaseFeature = -> Fillet006
  Direction = (0,0,-1)
  Length = 37.3
  Length2 = 10
  Profile = -> Sketch018
  ReferenceAxis = -> Sketch018 [N_Axis]
  Reversed = true
  SideType = 0
  Suppressed = false
  Type = 0
  Type2 = 0
  expr: Length = <<dim>>.total_depth - <<dim>>.rim_depth - <<dim>>.wall_thickness
FEATURE [PartDesign::Pocket] Pocket003  label="rim pocket"
  BaseFeature = -> Pad017
  Direction = (0,0,1)
  Length = 5.7
  Length2 = 5
  Profile = -> Sketch021
  ReferenceAxis = -> Sketch021 [N_Axis]
  SideType = 0
  Suppressed = false
  Type = 0
  Type2 = 0
  expr: Length = <<dim>>.rim_depth
FEATURE [PartDesign::Pad] Pad015  label="internal baffle pad"
  BaseFeature = -> Pocket003
  Direction = (0,0,-1)
  Length = 37.3
  Length2 = 10
  Profile = -> Sketch031
  ReferenceAxis = -> Sketch031 [N_Axis]
  SideType = 0
  Suppressed = false
  Type = 0
  Type2 = 0
  expr: Length = <<dim>>.total_depth - <<dim>>.rim_depth - <<dim>>.front_thickness
FEATURE [PartDesign::Pad] Pad002  label="bmr support pad"
  BaseFeature = -> Pad015
  Direction = (0,0,-1)
  Length = 5
  Length2 = 10
  Profile = -> Sketch008
  ReferenceAxis = -> Sketch008 [N_Axis]
  SideType = 0
  Suppressed = false
  Type = 0
  Type2 = 0
FEATURE [TechDraw::DrawSVGTemplate] Template
  Height = 210
  Orientation = 1
  Template = /Applications/FreeCAD.app/Contents/Resources/share/Mod/TechDraw/Templates/Default_Template_A4_Landscape.svg
  Width = 297
FEATURE [TechDraw::DrawProjGroupItem] View  label="Front"
  CoarseView = false
  Direction = (0,0,-1)
  Focus = 100
  HardHidden = false
  IsoCount = 0
  IsoHidden = false
  IsoVisible = false
  LockPosition = true
  Perspective = false
  Rotation = 0
  RotationVector = (1,0,0)
  Scale = 0.375
  ScaleType = 2
  ScrubCount = 1
  SeamHidden = false
  SeamVisible = false
  SmoothHidden = false
  SmoothVisible = true
  Source = -> [Hole008]
  Type = 0
  X = 0
  XDirection = (1e-16,1,0)
  Y = 0
FEATURE [TechDraw::DrawProjGroupItem] ProjItem  label="Bottom"
  CoarseView = false
  Direction = (-1,1e-16,0)
  Focus = 100
  HardHidden = false
  IsoCount = 0
  IsoHidden = false
  IsoVisible = false
  LockPosition = false
  Perspective = false
  Rotation = 0
  RotationVector = (1,0,0)
  Scale = 0.375
  ScaleType = 2
  ScrubCount = 1
  SeamHidden = false
  SeamVisible = false
  SmoothHidden = false
  SmoothVisible = true
  Source = -> [Hole008]
  Type = 5
  X = 0
  XDirection = (1e-16,1,0)
  Y = 52.3125
FEATURE [TechDraw::DrawProjGroup] ProjGroup
  Anchor = -> View
  AutoDistribute = true
  LockPosition = false
  ProjectionType = 0
  Rotation = 0
  Scale = 0.375
  ScaleType = 1
  Source = -> [Hole008]
  Views = -> [View,ProjItem]
  X = 150.061
  Y = 129.09
  spacingX = 15
  spacingY = 15
FEATURE [TechDraw::DrawViewDimExtent] DimExtent
  AngleOverride = false
  Arbitrary = false
  ArbitraryTolerances = false
  DirExtent = 0
  EqualTolerance = true
  ExtensionAngle = 0
  FormatSpec = %.2w
  FormatSpecOverTolerance = %+.2w
  FormatSpecUnderTolerance = %+.2w
  Inverted = false
  LineAngle = 0
  LockPosition = false
  MeasureType = 1
  OverTolerance = 0
  References2D = -> [View]
  Rotation = 0
  ScaleType = 0
  ShowUnits = false
  Source = -> [View]
  TheoreticalExact = false
  Type = 1
  UnderTolerance = 0
  UseActualArea = true
  X = 4.31269
  Y = -39.2603
FEATURE [TechDraw::DrawViewDimExtent] DimExtent001
  AngleOverride = false
  Arbitrary = false
  ArbitraryTolerances = false
  DirExtent = 1
  EqualTolerance = true
  ExtensionAngle = 0
  FormatSpec = %.2w
  FormatSpecOverTolerance = %+.2w
  FormatSpecUnderTolerance = %+.2w
  Inverted = false
  LineAngle = 0
  LockPosition = false
  MeasureType = 1
  OverTolerance = 0
  References2D = -> [View]
  Rotation = 0
  ScaleType = 0
  ShowUnits = false
  Source = -> [View]
  TheoreticalExact = false
  Type = 2
  UnderTolerance = 0
  UseActualArea = true
  X = 97.2585
  Y = -5.20496
FEATURE [TechDraw::DrawViewDimExtent] DimExtent002
  AngleOverride = false
  Arbitrary = false
  ArbitraryTolerances = false
  DirExtent = 1
  EqualTolerance = true
  ExtensionAngle = 0
  FormatSpec = %.2w
  FormatSpecOverTolerance = %+.2w
  FormatSpecUnderTolerance = %+.2w
  Inverted = false
  LineAngle = 0
  LockPosition = false
  MeasureType = 1
  OverTolerance = 0
  References2D = -> [ProjItem]
  Rotation = 0
  ScaleType = 0
  ShowUnits = false
  Source = -> [ProjItem]
  TheoreticalExact = false
  Type = 2
  UnderTolerance = 0
  UseActualArea = true
  X = 95.9201
  Y = -4.90754
FEATURE [TechDraw::DrawViewAnnotation] Annotation
  Font = osifont
  LineSpace = 100
  LockPosition = false
  MaxWidth = -1
  Rotation = 0
  ScaleType = 0
  Text = Corner | radius | 7mm
  TextSize = 3
  TextStyle = 0
  X = 48.3271
  Y = 98.1589
FEATURE [TechDraw::DrawViewImage] ActiveView
  Height = 102.4
  ImageFile = <userpath>/Library/Caches/FreeCAD/Cache/FreeCAD_Doc_b72852a3-4320-47ef-8016-d30b04bf8afa_456ddf_487194/PageActiveViewcDX8Vj.png
  LockPosition = false
  Rotation = 0
  ScaleType = 2
  Width = 128
  X = 98.6422
  Y = 59.5398
FEATURE [TechDraw::DrawSVGTemplate] Template002
  Height = 210
  Orientation = 1
  Template = /Applications/FreeCAD.app/Contents/Resources/share/Mod/TechDraw/Templates/Default_Template_A4_Landscape.svg
  Width = 297
FEATURE [PartDesign::Chamfer] Chamfer  label="bmr interior chamfer"
  Angle = 45
  Base = -> Pad002 [Edge163]
  BaseFeature = -> Pad002
  ChamferType = 0
  FlipDirection = false
  Size = 3
  Size2 = 1
  SupportTransform = false
  Suppressed = false
  UseAllEdges = false
FEATURE [PartDesign::Pad] Pad001  label="woofer support pad"
  BaseFeature = -> Chamfer
  Direction = (0,0,-1)
  Length = 7
  Length2 = 10
  Profile = -> Sketch003
  ReferenceAxis = -> Sketch003 [N_Axis]
  SideType = 0
  Suppressed = false
  Type = 0
  Type2 = 0
  expr: Length = <<dim>>.woofer_support_thickness
FEATURE [PartDesign::Pocket] Pocket  label="driver holes pocket"
  BaseFeature = -> Pad001
  Direction = (0,0,-1)
  Length = 5
  Length2 = 5
  Profile = -> Sketch001
  ReferenceAxis = -> Sketch001 [N_Axis]
  SideType = 0
  Suppressed = false
  Type = 1
  Type2 = 0
  expr: Length = <<dim>>.wall_thickness
FEATURE [PartDesign::Pocket] Pocket001  label="woofer rebate pocket"
  BaseFeature = -> Pocket
  Direction = (0,0,-1)
  Length = 8
  Length2 = 5
  Profile = -> Sketch002
  ReferenceAxis = -> Sketch002 [N_Axis]
  SideType = 0
  Suppressed = false
  Type = 0
  Type2 = 0
  expr: Length = <<dim>>.woofer_rebate_depth
FEATURE [PartDesign::Pocket] Pocket002  label="bmr rebate pocket"
  BaseFeature = -> Pocket001
  Direction = (0,0,-1)
  Length = 6
  Length2 = 5
  Profile = -> Sketch004
  ReferenceAxis = -> Sketch004 [N_Axis]
  SideType = 0
  Suppressed = false
  Type = 0
  Type2 = 0
  expr: Length = <<dim>>.bmr_rebate_depth
FEATURE [Sketcher::SketchObject] Sketch005  label="bmr screw positions"
  ArcFitTolerance = 1e-06
  AttachmentOffset = pos=(-45,0,0) rot=(0,0,1;0rad)
  AttachmentSupport = -> [Pocket002]
  ExternalTypes = [0]
  FullyConstrained = true
  MakeInternals = false
  MapMode = 5
  Placement = pos=(-45,0,42) rot=(0,0,1;0rad)
  expr: .AttachmentOffset.Base.x = -<<dim>>.bmr_x
  expr: .AttachmentOffset.Base.y = <<dim>>.bmr_y
  expr: Constraints[7] = <<dim>>.bmr_screw_offset
  expr: Constraints[8] = <<dim>>.bmr_screw_offset
  sketch-geometry (4):
    g0: Circle CenterX=16.95 CenterY=-16.95 CenterZ=0 NormalX=0 NormalY=0 NormalZ=1 AngleXU=0 Radius=1.6
    g1: Circle CenterX=16.95 CenterY=16.95 CenterZ=0 NormalX=0 NormalY=0 NormalZ=1 AngleXU=0 Radius=1.6
    g2: Circle CenterX=-16.95 CenterY=16.95 CenterZ=0 NormalX=0 NormalY=0 NormalZ=1 AngleXU=0 Radius=1.6
    g3: Circle CenterX=-16.95 CenterY=-16.95 CenterZ=0 NormalX=0 NormalY=0 NormalZ=1 AngleXU=0 Radius=1.6
  constraints (9):
    c: Equal(g0,g1)
    c: Equal(g0,g2)
    c: Equal(g0,g3)
    c: Diameter(g0) = 3.2
    c: Symmetric(g2,g1,g-2)
    c: Symmetric(g3,g0,g-2)
    c: Symmetric(g2,g3,g-1)
    c: DistanceX(g-1,g1) = 16.95
    c: DistanceY(g-1,g1) = 16.95
FEATURE [Sketcher::SketchObject] Sketch006  label="top woofer screw positions"
  ArcFitTolerance = 1e-06
  AttachmentOffset = pos=(0,120,0) rot=(0,0,1;0rad)
  AttachmentSupport = -> [Pocket001]
  ExternalTypes = [0]
  FullyConstrained = true
  MakeInternals = false
  MapMode = 5
  Placement = pos=(0,120,40) rot=(0,0,1;0rad)
  expr: .AttachmentOffset.Base.x = -<<dim>>.woofer_x
  expr: .AttachmentOffset.Base.y = <<dim>>.woofer_y
  expr: Constraints[7] = <<dim>>.woofer_screw_offset
  expr: Constraints[8] = <<dim>>.woofer_screw_offset
  sketch-geometry (4):
    g0: Circle CenterX=49.5253 CenterY=-49.5253 CenterZ=0 NormalX=0 NormalY=0 NormalZ=1 AngleXU=0 Radius=2
    g1: Circle CenterX=49.5253 CenterY=49.5253 CenterZ=0 NormalX=0 NormalY=0 NormalZ=1 AngleXU=0 Radius=2
    g2: Circle CenterX=-49.5253 CenterY=49.5253 CenterZ=0 NormalX=0 NormalY=0 NormalZ=1 AngleXU=0 Radius=2
    g3: Circle CenterX=-49.5253 CenterY=-49.5253 CenterZ=0 NormalX=0 NormalY=0 NormalZ=1 AngleXU=0 Radius=2
  constraints (9):
    c: Equal(g0,g1)
    c: Equal(g0,g2)
    c: Equal(g0,g3)
    c: Diameter(g0) = 4
    c: Symmetric(g2,g1,g-2)
    c: Symmetric(g3,g0,g-2)
    c: Symmetric(g2,g3,g-1)
    c: DistanceX(g-1,g1) = 49.5253
    c: DistanceY(g-1,g1) = 49.5253
FEATURE [Sketcher::SketchObject] Sketch007  label="bottom woofer screw positions"
  ArcFitTolerance = 1e-06
  AttachmentOffset = pos=(0,-120,0) rot=(0,0,1;0rad)
  AttachmentSupport = -> [Pocket001]
  ExternalTypes = [0]
  FullyConstrained = true
  MakeInternals = true
  MapMode = 5
  Placement = pos=(0,-120,40) rot=(0,0,1;0rad)
  expr: .AttachmentOffset.Base.x = -<<dim>>.woofer_x
  expr: .AttachmentOffset.Base.y = -<<dim>>.woofer_y
  expr: Constraints[7] = <<dim>>.woofer_screw_offset
  expr: Constraints[8] = <<dim>>.woofer_screw_offset
  sketch-geometry (4):
    g0: Circle CenterX=49.5253 CenterY=-49.5253 CenterZ=0 NormalX=0 NormalY=0 NormalZ=1 AngleXU=0 Radius=2
    g1: Circle CenterX=49.5253 CenterY=49.5253 CenterZ=0 NormalX=0 NormalY=0 NormalZ=1 AngleXU=0 Radius=2
    g2: Circle CenterX=-49.5253 CenterY=49.5253 CenterZ=0 NormalX=0 NormalY=0 NormalZ=1 AngleXU=0 Radius=2
    g3: Circle CenterX=-49.5253 CenterY=-49.5253 CenterZ=0 NormalX=0 NormalY=0 NormalZ=1 AngleXU=0 Radius=2
  constraints (9):
    c: Equal(g0,g1)
    c: Equal(g0,g2)
    c: Equal(g0,g3)
    c: Diameter(g0) = 4
    c: Symmetric(g2,g1,g-2)
    c: Symmetric(g3,g0,g-2)
    c: Symmetric(g2,g3,g-1)
    c: DistanceX(g-1,g1) = 49.5253
    c: DistanceY(g-1,g1) = 49.5253
FEATURE [TechDraw::DrawViewImage] ActiveView001
  Height = 102.4
  ImageFile = <userpath>/Library/Caches/FreeCAD/Cache/FreeCAD_Doc_b72852a3-4320-47ef-8016-d30b04bf8afa_456ddf_487194/Page002ActiveView001gEmG7B.png
  LockPosition = false
  Rotation = 0
  ScaleType = 2
  Width = 128
  X = 79.3706
  Y = 107.09
FEATURE [TechDraw::DrawViewImage] Image001
  Height = 100
  ImageFile = <userpath>/Downloads/Screenshot 2025-10-16 at 9.36.40 am.png
  LockPosition = false
  Rotation = 0
  ScaleType = 2
  Width = 100
  X = 189.42
  Y = 107.09
FEATURE [TechDraw::DrawViewAnnotation] Annotation004
  Font = osifont
  LineSpace = 100
  LockPosition = false
  MaxWidth = -1
  Owner = -> Image001
  Rotation = 0
  ScaleType = 0
  Text = Interior baffle detail
  TextSize = 5
  TextStyle = 0
  X = -44.403
  Y = 85.4975
FEATURE [TechDraw::DrawPage] Page002  label="Interior baffle detail"
  KeepUpdated = true
  NextBalloonIndex = 1
  ProjectionType = 0
  Template = -> Template002
  Views = -> [ActiveView001,Image001,Annotation004]
FEATURE [TechDraw::DrawViewAnnotation] Annotation005
  Font = osifont
  LineSpace = 100
  LockPosition = false
  MaxWidth = -1
  Rotation = 0
  ScaleType = 0
  Text = Back panel dimensions
  TextSize = 5
  TextStyle = 0
  X = 150.061
  Y = 195.264
FEATURE [TechDraw::DrawPage] Page  label="Back panel"
  KeepUpdated = true
  NextBalloonIndex = 1
  ProjectionType = 0
  Template = -> Template
  Views = -> [ProjGroup,DimExtent,DimExtent001,DimExtent002,Annotation,ActiveView,Annotation005]
FEATURE [TechDraw::DrawSVGTemplate] Template003
  Height = 210
  Orientation = 1
  Template = /Applications/FreeCAD.app/Contents/Resources/share/Mod/TechDraw/Templates/Default_Template_A4_Landscape.svg
  Width = 297
FEATURE [TechDraw::DrawViewAnnotation] Annotation006
  Font = osifont
  LineSpace = 100
  LockPosition = false
  MaxWidth = -1
  Rotation = 0
  ScaleType = 0
  Text = Sections through driver cutouts
  TextSize = 5
  TextStyle = 0
  X = 139.794
  Y = 200.103
FEATURE [TechDraw::DrawPage] Page003  label="Driver cutout sections"
  KeepUpdated = true
  NextBalloonIndex = 1
  ProjectionType = 0
  Template = -> Template003
  Views = -> [Annotation006]
FEATURE [TechDraw::DrawSVGTemplate] Template004
  Height = 210
  Orientation = 1
  Template = /Applications/FreeCAD.app/Contents/Resources/share/Mod/TechDraw/Templates/Default_Template_A4_Landscape.svg
  Width = 297
FEATURE [TechDraw::DrawViewImage] Image002
  Height = 100
  ImageFile = <userpath>/Downloads/Screenshot 2025-10-16 at 10.15.59 am.png
  LockPosition = false
  Rotation = 0
  Scale = 0.3
  ScaleType = 2
  Width = 100
  X = 59.6084
  Y = 146.498
FEATURE [TechDraw::DrawViewImage] Image003
  Height = 100
  ImageFile = <userpath>/Downloads/Screenshot 2025-10-16 at 10.15.02 am.png
  LockPosition = false
  Rotation = 0
  ScaleType = 2
  Width = 100
  X = 139.377
  Y = 80.7295
FEATURE [TechDraw::DrawViewAnnotation] Annotation007
  Font = osifont
  LineSpace = 100
  LockPosition = false
  MaxWidth = -1
  Owner = -> Image002
  Rotation = 0
  ScaleType = 0
  Text = Driver holes layout
  TextSize = 5
  TextStyle = 0
  X = 79.7687
  Y = 47.5082
FEATURE [TechDraw::DrawPage] Page004  label="Driver holes layout"
  KeepUpdated = true
  NextBalloonIndex = 1
  ProjectionType = 0
  Template = -> Template004
  Views = -> [Image002,Image003,Annotation007]
FEATURE [PartDesign::Chamfer] Chamfer003  label="Front driver hole chamfers"
  Angle = 45
  Base = -> Pocket002 [Edge46,Edge25,Edge45]
  BaseFeature = -> Pocket002
  ChamferType = 0
  FlipDirection = false
  Size = 1.5
  Size2 = 1
  SupportTransform = false
  Suppressed = false
  UseAllEdges = false
FEATURE [PartDesign::Hole] Hole  label="bmr screw holes"
  BaseFeature = -> Chamfer003
  BaseProfileType = 6
  CustomThreadClearance = 0
  Depth = 25
  DepthType = 0
  Diameter = 2.52
  DrillForDepth = false
  DrillPoint = 1
  DrillPointAngle = 118
  HoleCutCountersinkAngle = 90
  HoleCutCustomValues = false
  HoleCutDepth = 0
  HoleCutDiameter = 6.1
  HoleCutType = 0
  ModelThread = true
  Profile = -> Sketch005
  Suppressed = false
  Tapered = false
  TaperedAngle = 90
  ThreadClass = 0
  ThreadDepth = 25
  ThreadDepthType = 0
  ThreadDiameter = 3
  ThreadDirection = 0
  ThreadFit = 0
  ThreadSize = 9
  ThreadType = 1
  Threaded = true
  UseCustomThreadClearance = false
FEATURE [PartDesign::Hole] Hole001  label="top woofer screw holes"
  BaseFeature = -> Hole
  BaseProfileType = 6
  CustomThreadClearance = 0
  Depth = 25
  DepthType = 0
  Diameter = 3.322
  DrillForDepth = false
  DrillPoint = 1
  DrillPointAngle = 118
  HoleCutCountersinkAngle = 90
  HoleCutCustomValues = false
  HoleCutDepth = 0
  HoleCutDiameter = 6.1
  HoleCutType = 0
  ModelThread = true
  Profile = -> Sketch006
  Suppressed = false
  Tapered = false
  TaperedAngle = 90
  ThreadClass = 0
  ThreadDepth = 10
  ThreadDepthType = 1
  ThreadDiameter = 4
  ThreadDirection = 0
  ThreadFit = 0
  ThreadSize = 11
  ThreadType = 1
  Threaded = true
  UseCustomThreadClearance = false
FEATURE [PartDesign::Hole] Hole002  label="bottom woofer screw holes"
  BaseFeature = -> Hole001
  BaseProfileType = 6
  CustomThreadClearance = 0
  Depth = 25
  DepthType = 0
  Diameter = 3.322
  DrillForDepth = false
  DrillPoint = 1
  DrillPointAngle = 118
  HoleCutCountersinkAngle = 90
  HoleCutCustomValues = false
  HoleCutDepth = 0
  HoleCutDiameter = 6.1
  HoleCutType = 0
  ModelThread = true
  Profile = -> Sketch007
  Suppressed = false
  Tapered = false
  TaperedAngle = 90
  ThreadClass = 0
  ThreadDepth = 25
  ThreadDepthType = 0
  ThreadDiameter = 4
  ThreadDirection = 0
  ThreadFit = 0
  ThreadSize = 11
  ThreadType = 1
  Threaded = true
  UseCustomThreadClearance = false
FEATURE [PartDesign::Hole] Hole007  label="back panel post screw holes"
  BaseFeature = -> Hole002
  BaseProfileType = 7
  CustomThreadClearance = 0
  Depth = 20
  DepthType = 0
  Diameter = 3.322
  DrillForDepth = false
  DrillPoint = 1
  DrillPointAngle = 118
  HoleCutCountersinkAngle = 90
  HoleCutCustomValues = false
  HoleCutDepth = 0
  HoleCutDiameter = 0
  HoleCutType = 0
  ModelThread = true
  Profile = -> Sketch018
  Suppressed = false
  Tapered = false
  TaperedAngle = 90
  ThreadClass = 0
  ThreadDepth = 20
  ThreadDepthType = 0
  ThreadDiameter = 4
  ThreadDirection = 0
  ThreadFit = 0
  ThreadSize = 11
  ThreadType = 1
  Threaded = true
  UseCustomThreadClearance = false
FEATURE [PartDesign::Fillet] Fillet  label="Exterior roundovers"
  Base = -> Hole007 [Edge30,Edge31,Edge28,Edge29,Edge80,Edge82,Edge77,Edge78]
  BaseFeature = -> Hole007
  Radius = 10
  SupportTransform = false
  Suppressed = false
  UseAllEdges = false
FEATURE [PartDesign::Body] Body  label="main shell"
  AllowCompound = false
  Group = -> [Sketch,Pad,Thickness001,Fillet006,Pad017,Pocket003,Pad015,Pad002,Chamfer,Pad001,Pocket,Sketch001,Sketch002,Pocket001,Sketch003,Sketch004,Pocket002,Chamfer003,Sketch005,Hole,Sketch006,Hole001,Sketch007,Hole002,Sketch008,Sketch018,Sketch021,Sketch031,Hole007,Fillet]
  Origin = -> Origin
  Tip = -> Fillet
FEATURE [App::Point] Origin021
  Role = Origin
FEATURE [Sketcher::SketchObject] Sketch033
  ArcFitTolerance = 1e-06
  AttachmentOffset = pos=(0,0,5.8) rot=(0,0,1;0rad)
  AttachmentSupport = -> [Origin020]
  ExternalTypes = [0]
  FullyConstrained = true
  MakeInternals = false
  MapMode = 5
  Placement = pos=(0,0,5.8) rot=(0,0,1;0rad)
  sketch-geometry (16):
    g0: LineSegment StartX=-22.5 StartY=-92.5 StartZ=0 EndX=-22.5 EndY=-157.5 EndZ=0
    g1: LineSegment StartX=-22.5 StartY=-157.5 StartZ=0 EndX=22.5 EndY=-157.5 EndZ=0
    g2: LineSegment StartX=22.5 StartY=-157.5 StartZ=0 EndX=22.5 EndY=-92.5 EndZ=0
    g3: LineSegment StartX=22.5 StartY=-92.5 StartZ=0 EndX=-22.5 EndY=-92.5 EndZ=0
    g4: LineSegment StartX=-72.5 StartY=32.5 StartZ=0 EndX=-72.5 EndY=-32.5 EndZ=0
    g5: LineSegment StartX=-72.5 StartY=-32.5 StartZ=0 EndX=-27.5 EndY=-32.5 EndZ=0
    g6: LineSegment StartX=-27.5 StartY=-32.5 StartZ=0 EndX=-27.5 EndY=32.5 EndZ=0
    g7: LineSegment StartX=-27.5 StartY=32.5 StartZ=0 EndX=-72.5 EndY=32.5 EndZ=0
    g8: LineSegment StartX=27.5 StartY=32.5 StartZ=0 EndX=27.5 EndY=-32.5 EndZ=0
    g9: LineSegment StartX=27.5 StartY=-32.5 StartZ=0 EndX=72.5 EndY=-32.5 EndZ=0
    g10: LineSegment StartX=72.5 StartY=-32.5 StartZ=0 EndX=72.5 EndY=32.5 EndZ=0
    g11: LineSegment StartX=72.5 StartY=32.5 StartZ=0 EndX=27.5 EndY=32.5 EndZ=0
    g12: LineSegment StartX=-22.5 StartY=157.5 StartZ=0 EndX=-22.5 EndY=92.5 EndZ=0
    g13: LineSegment StartX=-22.5 StartY=92.5 StartZ=0 EndX=22.5 EndY=92.5 EndZ=0
    g14: LineSegment StartX=22.5 StartY=92.5 StartZ=0 EndX=22.5 EndY=157.5 EndZ=0
    g15: LineSegment StartX=22.5 StartY=157.5 StartZ=0 EndX=-22.5 EndY=157.5 EndZ=0
  constraints (42):
    c: Coincident(g0,g1)
    c: Coincident(g1,g2)
    c: Coincident(g2,g3)
    c: Coincident(g3,g0)
    c: Vertical(g0)
    c: Vertical(g2)
    c: Horizontal(g1)
    c: DistanceX(g3,g3) = 45
    c: DistanceY(g0,g0) = 65
    c: Coincident(g4,g5)
    c: Coincident(g5,g6)
    c: Coincident(g6,g7)
    c: Coincident(g7,g4)
    c: Vertical(g4)
    c: Horizontal(g5)
    c: Horizontal(g7)
    c: DistanceX(g7,g7) = 45
    c: DistanceY(g4,g4) = 65
    c: Coincident(g8,g9)
    c: Coincident(g9,g10)
    c: Coincident(g10,g11)
    c: Coincident(g11,g8)
    c: Vertical(g10)
    c: Horizontal(g9)
    c: Horizontal(g11)
    c: DistanceX(g11,g11) = 45
    c: Coincident(g12,g13)
    c: Coincident(g13,g14)
    c: Coincident(g14,g15)
    c: Coincident(g15,g12)
    c: Vertical(g12)
    c: Vertical(g14)
    c: Horizontal(g13)
    c: DistanceY(g12,g12) = 65
    c: Symmetric(g12,g14,g-2)
    c: Symmetric(g6,g5,g-1)
    c: Symmetric(g8,g8,g-1)
    c: Symmetric(g2,g0,g-2)
    c: DistanceX(g6,g8) = 55
    c: Symmetric(g6,g8,g-2)
    c: Symmetric(g13,g2,g-1)
    c: DistanceY(g2,g13) = 185
FEATURE [PartDesign::Pad] Pad018
  Direction = (0,0,1)
  Length = 0.55
  Length2 = 10
  Profile = -> Sketch033
  ReferenceAxis = -> Sketch033 [N_Axis]
  SideType = 0
  Suppressed = false
  Type = 0
  Type2 = 0
FEATURE [PartDesign::Body] Body009  label="CLD tiles"
  AllowCompound = true
  Group = -> [Sketch033,Pad018]
  Origin = -> Origin020
  Tip = -> Pad018
FEATURE [App::Point] Origin023
  Role = Origin
FEATURE [PartDesign::SubShapeBinder] Binder
  BindCopyOnChange = 0
  BindMode = 0
  ClaimChildren = false
  Context = -> Body010 [Binder.]
  Fuse = false
  MakeFace = true
  OffsetFill = false
  OffsetIntersection = false
  OffsetJoinType = 0
  OffsetOpenResult = false
  PartialLoad = false
  Refine = true
  Relative = true
  Support = -> [Body002[Hole008.Face5]]
  _Version = 2
FEATURE [PartDesign::Pad] Pad019
  Direction = (0,0,1)
  Length = 0.8
  Length2 = 10
  Profile = -> Binder
  SideType = 0
  Suppressed = false
  Type = 0
  Type2 = 0
FEATURE [PartDesign::Body] Body010  label="back panel gasket"
  AllowCompound = false
  Group = -> [Binder,Pad019]
  Origin = -> Origin022
  Tip = -> Pad019
FEATURE [App::DocumentObjectGroup] Group002  label="Gaskets"
  Group = -> [Body004,Body007,Body010]
FEATURE [PartDesign::Pad] Pad020
  Direction = (0,0,1)
  Length = 4
  Length2 = 10
  Profile = -> Sketch027
  ReferenceAxis = -> Sketch027 [N_Axis]
  SideType = 0
  Suppressed = false
  Type = 0
  Type2 = 0
FEATURE [PartDesign::Chamfer] Chamfer004
  Angle = 45
  Base = -> Pad020 [Edge10]
  BaseFeature = -> Pad020
  ChamferType = 1
  FlipDirection = false
  Size = 0.4
  Size2 = 6.6
  SupportTransform = false
  Suppressed = false
  UseAllEdges = false
FEATURE [PartDesign::Pocket] Pocket005
  BaseFeature = -> Chamfer004
  Direction = (0,0,-1)
  Length = 5
  Length2 = 5
  Profile = -> Sketch015
  ReferenceAxis = -> Sketch015 [N_Axis]
  Reversed = true
  SideType = 0
  Suppressed = false
  Type = 0
  Type2 = 0
FEATURE [PartDesign::PolarPattern] PolarPattern
  Angle = 360
  Axis = -> Z_Axis003
  BaseFeature = -> Pocket005
  Mode = 0
  Occurrences = 4
  Offset = 120
  SpacingPattern = [0]
  Spacings = [-1,-1,-1]
  Suppressed = false
  TransformMode = 1
FEATURE [PartDesign::Body] Body003  label="Tweeter ring"
  AllowCompound = false
  Group = -> [Sketch015,Sketch027,Pad020,Chamfer004,Pocket005,PolarPattern]
  Origin = -> Origin006
  Placement = pos=(-45,0,42.7) rot=(0,0,1;0rad)
  Tip = -> PolarPattern
FEATURE [TechDraw::DrawSVGTemplate] Template005
  Height = 210
  Orientation = 1
  Template = /Applications/FreeCAD.app/Contents/Resources/share/Mod/TechDraw/Templates/Default_Template_A4_Landscape.svg
  Width = 297
FEATURE [TechDraw::DrawProjGroupItem] View001
  CoarseView = false
  Direction = (0,0,1)
  Focus = 100
  HardHidden = false
  IsoCount = 0
  IsoHidden = false
  IsoVisible = false
  LockPosition = false
  Perspective = false
  Rotation = 0
  RotationVector = (1,0,0)
  Scale = 0.5
  ScaleType = 2
  ScrubCount = 1
  SeamHidden = false
  SeamVisible = false
  SmoothHidden = false
  SmoothVisible = true
  Source = -> [Sketch,Sketch005,Sketch006,Sketch007,Sketch018]
  Type = 0
  X = 148.5
  XDirection = (1e-16,-1,0)
  Y = 105
FEATURE [TechDraw::DrawViewDimension] Dimension
  AngleOverride = false
  Arbitrary = false
  ArbitraryTolerances = false
  BoxCorners = (2) [(-125,-50,0),(125,50,0)]
  EqualTolerance = true
  ExtensionAngle = 0
  FormatSpec = %.2w
  FormatSpecOverTolerance = %+.2w
  FormatSpecUnderTolerance = %+.2w
  Inverted = false
  LineAngle = 0
  LockPosition = false
  MeasureType = 1
  OverTolerance = 0
  References2D = -> [View001]
  Rotation = 0
  ScaleType = 0
  ShowUnits = false
  TheoreticalExact = false
  Type = 2
  UnderTolerance = 0
  UseActualArea = true
  X = -139.016
  Y = 47.75
FEATURE [TechDraw::DrawViewDimension] Dimension001
  AngleOverride = false
  Arbitrary = false
  ArbitraryTolerances = false
  BoxCorners = (2) [(-125,-50,0),(125,50,0)]
  EqualTolerance = true
  ExtensionAngle = 0
  FormatSpec = %.2w
  FormatSpecOverTolerance = %+.2w
  FormatSpecUnderTolerance = %+.2w
  Inverted = false
  LineAngle = 0
  LockPosition = false
  MeasureType = 1
  OverTolerance = 0
  References2D = -> [View001]
  Rotation = 0
  ScaleType = 0
  ShowUnits = false
  TheoreticalExact = false
  Type = 1
  UnderTolerance = 0
  UseActualArea = true
  X = -122.75
  Y = 60.7881
FEATURE [TechDraw::DrawViewDimension] Dimension002
  AngleOverride = false
  Arbitrary = false
  ArbitraryTolerances = false
  BoxCorners = (2) [(-125,-50,0),(125,50,0)]
  EqualTolerance = true
  ExtensionAngle = 0
  FormatSpec = %.2w
  FormatSpecOverTolerance = %+.2w
  FormatSpecUnderTolerance = %+.2w
  Inverted = false
  LineAngle = 0
  LockPosition = false
  MeasureType = 1
  OverTolerance = 0
  References2D = -> [View001]
  Rotation = 0
  ScaleType = 0
  ShowUnits = false
  TheoreticalExact = false
  Type = 0
  UnderTolerance = 0
  UseActualArea = true
  X = -85.8252
  Y = 75.4627
FEATURE [TechDraw::DrawViewDimension] Dimension003
  AngleOverride = false
  Arbitrary = false
  ArbitraryTolerances = false
  BoxCorners = (2) [(-125,-50,0),(125,50,0)]
  EqualTolerance = true
  ExtensionAngle = 0
  FormatSpec = %.2w
  FormatSpecOverTolerance = %+.2w
  FormatSpecUnderTolerance = %+.2w
  Inverted = false
  LineAngle = 0
  LockPosition = false
  MeasureType = 1
  OverTolerance = 0
  References2D = -> [View001]
  Rotation = 0
  ScaleType = 0
  ShowUnits = false
  TheoreticalExact = false
  Type = 0
  UnderTolerance = 0
  UseActualArea = true
  X = 126.966
  Y = 75.4627
FEATURE [TechDraw::DrawViewDimension] Dimension004
  AngleOverride = false
  Arbitrary = false
  ArbitraryTolerances = false
  BoxCorners = (2) [(-125,-50,0),(125,50,0)]
  EqualTolerance = true
  ExtensionAngle = 0
  FormatSpec = %.2w
  FormatSpecOverTolerance = %+.2w
  FormatSpecUnderTolerance = %+.2w
  Inverted = false
  LineAngle = 0
  LockPosition = false
  MeasureType = 1
  OverTolerance = 0
  References2D = -> [View001]
  Rotation = 0
  ScaleType = 0
  ShowUnits = false
  TheoreticalExact = false
  Type = 0
  UnderTolerance = 0
  UseActualArea = true
  X = 122.75
  Y = 59.1621
FEATURE [TechDraw::DrawViewDimension] Dimension009
  AngleOverride = false
  Arbitrary = false
  ArbitraryTolerances = false
  BoxCorners = (2) [(-125,-50,0),(125,50,0)]
  EqualTolerance = true
  ExtensionAngle = 0
  FormatSpec = %.2w
  FormatSpecOverTolerance = %+.2w
  FormatSpecUnderTolerance = %+.2w
  Inverted = false
  LineAngle = 0
  LockPosition = false
  MeasureType = 1
  OverTolerance = 0
  References2D = -> [View001]
  Rotation = 0
  ScaleType = 0
  ShowUnits = false
  TheoreticalExact = false
  Type = 2
  UnderTolerance = 0
  UseActualArea = true
  X = -79.1317
  Y = 37.3813
FEATURE [TechDraw::DrawViewDimension] Dimension010
  AngleOverride = false
  Arbitrary = false
  ArbitraryTolerances = false
  BoxCorners = (2) [(-125,-50,0),(125,50,0)]
  EqualTolerance = true
  ExtensionAngle = 0
  FormatSpec = %.2w
  FormatSpecOverTolerance = %+.2w
  FormatSpecUnderTolerance = %+.2w
  Inverted = false
  LineAngle = 0
  LockPosition = false
  MeasureType = 1
  OverTolerance = 0
  References2D = -> [View001]
  Rotation = 0
  ScaleType = 0
  ShowUnits = false
  TheoreticalExact = false
  Type = 1
  UnderTolerance = 0
  UseActualArea = true
  X = -104.881
  Y = 21.079
FEATURE [TechDraw::DrawViewDimension] Dimension016
  AngleOverride = false
  Arbitrary = false
  ArbitraryTolerances = false
  BoxCorners = (2) [(-125,-50,0),(125,50,0)]
  EqualTolerance = true
  ExtensionAngle = 0
  FormatSpec = %.2w
  FormatSpecOverTolerance = %+.2w
  FormatSpecUnderTolerance = %+.2w
  Inverted = false
  LineAngle = 0
  LockPosition = false
  MeasureType = 1
  OverTolerance = 0
  References2D = -> [View001]
  Rotation = 0
  ScaleType = 0
  ShowUnits = false
  TheoreticalExact = false
  Type = 2
  UnderTolerance = 0
  UseActualArea = true
  X = 5.89192
  Y = 28.125
FEATURE [TechDraw::DrawViewDimension] Dimension017
  AngleOverride = false
  Arbitrary = false
  ArbitraryTolerances = false
  BoxCorners = (2) [(-125,-50,0),(125,50,0)]
  EqualTolerance = true
  ExtensionAngle = 0
  FormatSpec = %.2w
  FormatSpecOverTolerance = %+.2w
  FormatSpecUnderTolerance = %+.2w
  Inverted = false
  LineAngle = 0
  LockPosition = false
  MeasureType = 1
  OverTolerance = 0
  References2D = -> [View001]
  Rotation = 0
  ScaleType = 0
  ShowUnits = false
  TheoreticalExact = false
  Type = 2
  UnderTolerance = 0
  UseActualArea = true
  X = 131.702
  Y = -3.03332
FEATURE [TechDraw::DrawViewDimension] Dimension018
  AngleOverride = false
  Arbitrary = false
  ArbitraryTolerances = false
  BoxCorners = (2) [(-125,-50,0),(125,50,0)]
  EqualTolerance = true
  ExtensionAngle = 0
  FormatSpec = %.2w
  FormatSpecOverTolerance = %+.2w
  FormatSpecUnderTolerance = %+.2w
  Inverted = false
  LineAngle = 0
  LockPosition = false
  MeasureType = 1
  OverTolerance = 0
  References2D = -> [View001]
  Rotation = 0
  ScaleType = 0
  ShowUnits = false
  TheoreticalExact = false
  Type = 1
  UnderTolerance = 0
  UseActualArea = true
  X = -16.2483
  Y = -64.2187
FEATURE [TechDraw::DrawViewDimension] Dimension020
  AngleOverride = false
  Arbitrary = false
  ArbitraryTolerances = false
  BoxCorners = (2) [(-125,-50,0),(125,50,0)]
  EqualTolerance = true
  ExtensionAngle = 0
  FormatSpec = %.2w
  FormatSpecOverTolerance = %+.2w
  FormatSpecUnderTolerance = %+.2w
  Inverted = false
  LineAngle = 0
  LockPosition = false
  MeasureType = 1
  OverTolerance = 0
  References2D = -> [View001]
  Rotation = 0
  ScaleType = 0
  ShowUnits = false
  TheoreticalExact = false
  Type = 1
  UnderTolerance = 0
  UseActualArea = true
  X = 104.881
  Y = 18.9799
FEATURE [TechDraw::DrawViewDimension] Dimension021
  AngleOverride = false
  Arbitrary = false
  ArbitraryTolerances = false
  BoxCorners = (2) [(-125,-50,0),(125,50,0)]
  EqualTolerance = true
  ExtensionAngle = 0
  FormatSpec = %.2w
  FormatSpecOverTolerance = %+.2w
  FormatSpecUnderTolerance = %+.2w
  Inverted = false
  LineAngle = 0
  LockPosition = false
  MeasureType = 1
  OverTolerance = 0
  References2D = -> [View001]
  Rotation = 0
  ScaleType = 0
  ShowUnits = false
  TheoreticalExact = false
  Type = 1
  UnderTolerance = 0
  UseActualArea = true
  X = 60
  Y = 37.4616
FEATURE [TechDraw::DrawViewDimension] Dimension023
  AngleOverride = false
  Arbitrary = false
  ArbitraryTolerances = false
  BoxCorners = (2) [(-125,-50,0),(125,50,0)]
  EqualTolerance = true
  ExtensionAngle = 0
  FormatSpec = %.2w
  FormatSpecOverTolerance = %+.2w
  FormatSpecUnderTolerance = %+.2w
  Inverted = false
  LineAngle = 0
  LockPosition = false
  MeasureType = 1
  OverTolerance = 0
  References2D = -> [View001]
  Rotation = 0
  ScaleType = 0
  ShowUnits = false
  TheoreticalExact = false
  Type = 2
  UnderTolerance = 0
  UseActualArea = true
  X = -22.2228
  Y = -32.0125
FEATURE [TechDraw::DrawViewDimension] Dimension025
  AngleOverride = false
  Arbitrary = false
  ArbitraryTolerances = false
  BoxCorners = (2) [(-125,-50,0),(125,50,0)]
  EqualTolerance = true
  ExtensionAngle = 0
  FormatSpec = %.2w
  FormatSpecOverTolerance = %+.2w
  FormatSpecUnderTolerance = %+.2w
  Inverted = false
  LineAngle = 0
  LockPosition = false
  MeasureType = 1
  OverTolerance = 0
  References2D = -> [View001]
  Rotation = 0
  ScaleType = 0
  ShowUnits = false
  TheoreticalExact = false
  Type = 2
  UnderTolerance = 0
  UseActualArea = true
  X = 25.1153
  Y = 0
FEATURE [TechDraw::DrawViewDimension] Dimension026
  AngleOverride = false
  Arbitrary = false
  ArbitraryTolerances = false
  BoxCorners = (2) [(-125,-50,0),(125,50,0)]
  EqualTolerance = true
  ExtensionAngle = 0
  FormatSpec = %.2w
  FormatSpecOverTolerance = %+.2w
  FormatSpecUnderTolerance = %+.2w
  Inverted = false
  LineAngle = 0
  LockPosition = false
  MeasureType = 1
  OverTolerance = 0
  References2D = -> [View001]
  Rotation = 0
  ScaleType = 0
  ShowUnits = false
  TheoreticalExact = false
  Type = 2
  UnderTolerance = 0
  UseActualArea = true
  X = 90.0503
  Y = 37.3813
FEATURE [TechDraw::DrawViewDimension] Dimension027
  AngleOverride = false
  Arbitrary = false
  ArbitraryTolerances = false
  BoxCorners = (2) [(-125,-50,0),(125,50,0)]
  EqualTolerance = true
  ExtensionAngle = 0
  FormatSpec = %.2w
  FormatSpecOverTolerance = %+.2w
  FormatSpecUnderTolerance = %+.2w
  Inverted = false
  LineAngle = 0
  LockPosition = false
  MeasureType = 1
  OverTolerance = 0
  References2D = -> [View001]
  Rotation = 0
  ScaleType = 0
  ShowUnits = false
  TheoreticalExact = false
  Type = 0
  UnderTolerance = 0
  UseActualArea = true
  X = -139.016
  Y = -56.5871
FEATURE [TechDraw::DrawViewDimension] Dimension028
  AngleOverride = false
  Arbitrary = false
  ArbitraryTolerances = false
  BoxCorners = (2) [(-125,-50,0),(125,50,0)]
  EqualTolerance = true
  ExtensionAngle = 0
  FormatSpec = %.2w
  FormatSpecOverTolerance = %+.2w
  FormatSpecUnderTolerance = %+.2w
  Inverted = false
  LineAngle = 0
  LockPosition = false
  MeasureType = 1
  OverTolerance = 0
  References2D = -> [View001]
  Rotation = 0
  ScaleType = 0
  ShowUnits = false
  TheoreticalExact = false
  Type = 0
  UnderTolerance = 0
  UseActualArea = true
  X = -114.683
  Y = -57.2187
FEATURE [TechDraw::DrawViewDimension] Dimension029
  AngleOverride = false
  Arbitrary = false
  ArbitraryTolerances = false
  BoxCorners = (2) [(-125,-50,0),(125,50,0)]
  EqualTolerance = true
  ExtensionAngle = 0
  FormatSpec = %.2w
  FormatSpecOverTolerance = %+.2w
  FormatSpecUnderTolerance = %+.2w
  Inverted = false
  LineAngle = 0
  LockPosition = false
  MeasureType = 1
  OverTolerance = 0
  References2D = -> [View001]
  Rotation = 0
  ScaleType = 0
  ShowUnits = false
  TheoreticalExact = false
  Type = 1
  UnderTolerance = 0
  UseActualArea = true
  X = 122.75
  Y = -53.1031
FEATURE [TechDraw::DrawViewDimension] Dimension030
  AngleOverride = false
  Arbitrary = false
  ArbitraryTolerances = false
  BoxCorners = (2) [(-125,-50,0),(125,50,0)]
  EqualTolerance = true
  ExtensionAngle = 0
  FormatSpec = ⌀%.0w
  FormatSpecOverTolerance = %+.2w
  FormatSpecUnderTolerance = %+.2w
  Inverted = false
  LineAngle = 0
  LockPosition = false
  MeasureType = 1
  OverTolerance = 0
  References2D = -> [View001]
  Rotation = 0
  ScaleType = 0
  ShowUnits = false
  TheoreticalExact = false
  Type = 5
  UnderTolerance = 0
  UseActualArea = true
  X = -105.158
  Y = 6.83029
FEATURE [TechDraw::DrawViewDimension] Dimension031
  AngleOverride = false
  Arbitrary = false
  ArbitraryTolerances = false
  BoxCorners = (2) [(-125,-50,0),(125,50,0)]
  EqualTolerance = true
  ExtensionAngle = 0
  FormatSpec = ⌀%.0w
  FormatSpecOverTolerance = %+.2w
  FormatSpecUnderTolerance = %+.2w
  Inverted = false
  LineAngle = 0
  LockPosition = false
  MeasureType = 1
  OverTolerance = 0
  References2D = -> [View001]
  Rotation = 0
  ScaleType = 0
  ShowUnits = false
  TheoreticalExact = false
  Type = 5
  UnderTolerance = 0
  UseActualArea = true
  X = 18.3564
  Y = -17.6449
FEATURE [TechDraw::DrawViewDimension] Dimension032
  AngleOverride = false
  Arbitrary = false
  ArbitraryTolerances = false
  BoxCorners = (2) [(-125,-50,0),(125,50,0)]
  EqualTolerance = true
  ExtensionAngle = 0
  FormatSpec = ⌀%.0w
  FormatSpecOverTolerance = %+.2w
  FormatSpecUnderTolerance = %+.2w
  Inverted = false
  LineAngle = 0
  LockPosition = false
  MeasureType = 1
  OverTolerance = 0
  References2D = -> [View001]
  Rotation = 0
  ScaleType = 0
  ShowUnits = false
  TheoreticalExact = false
  Type = 5
  UnderTolerance = 0
  UseActualArea = true
  X = 106.866
  Y = 6.68799
FEATURE [TechDraw::DrawViewDimension] Dimension033
  AngleOverride = false
  Arbitrary = false
  ArbitraryTolerances = false
  BoxCorners = (2) [(-125,-50,0),(125,50,0)]
  EqualTolerance = true
  ExtensionAngle = 0
  FormatSpec = %.2w
  FormatSpecOverTolerance = %+.2w
  FormatSpecUnderTolerance = %+.2w
  Inverted = false
  LineAngle = 0
  LockPosition = false
  MeasureType = 1
  OverTolerance = 0
  References2D = -> [View001]
  Rotation = 0
  ScaleType = 0
  ShowUnits = false
  TheoreticalExact = false
  Type = 1
  UnderTolerance = 0
  UseActualArea = true
  X = 79.375
  Y = -60.1031
FEATURE [TechDraw::DrawViewDimension] Dimension034
  AngleOverride = false
  Arbitrary = false
  ArbitraryTolerances = false
  BoxCorners = (2) [(-125,-50,0),(125,50,0)]
  EqualTolerance = true
  ExtensionAngle = 0
  FormatSpec = %.2w
  FormatSpecOverTolerance = %+.2w
  FormatSpecUnderTolerance = %+.2w
  Inverted = false
  LineAngle = 0
  LockPosition = false
  MeasureType = 1
  OverTolerance = 0
  References2D = -> [View001]
  Rotation = 0
  ScaleType = 0
  ShowUnits = false
  TheoreticalExact = false
  Type = 1
  UnderTolerance = 0
  UseActualArea = true
  X = -79.375
  Y = -60.1031
FEATURE [TechDraw::DrawViewAnnotation] Annotation012
  Font = osifont
  LineSpace = 100
  LockPosition = false
  MaxWidth = -1
  Owner = -> View001
  Rotation = 0
  ScaleType = 0
  Text = threaded | M4 thru
  TextSize = 4
  TextStyle = 0
  X = -62.0418
  Y = -8.68016
FEATURE [TechDraw::DrawViewAnnotation] Annotation013
  Font = osifont
  LineSpace = 100
  LockPosition = false
  MaxWidth = -1
  Owner = -> View001
  Rotation = 0
  ScaleType = 0
  Text = threaded | M4 thru
  TextSize = 4
  TextStyle = 0
  X = 60.3342
  Y = -8.68016
FEATURE [TechDraw::DrawViewAnnotation] Annotation014
  Font = osifont
  LineSpace = 100
  LockPosition = false
  MaxWidth = -1
  Owner = -> View001
  Rotation = 0
  ScaleType = 0
  Text = threaded | M3 thru
  TextSize = 4
  TextStyle = 0
  X = 0
  Y = -21.4869
FEATURE [TechDraw::DrawViewAnnotation] Annotation015
  Font = osifont
  LineSpace = 100
  LockPosition = false
  MaxWidth = -1
  Owner = -> View001
  Rotation = 0
  ScaleType = 0
  Text = Perimeter holes | are threaded M4x20
  TextSize = 4
  TextStyle = 0
  X = 0
  Y = 64.0339
FEATURE [TechDraw::DrawViewDimension] Dimension035
  AngleOverride = false
  Arbitrary = false
  ArbitraryTolerances = false
  BoxCorners = (2) [(-125,-50,0),(125,50,0)]
  EqualTolerance = true
  ExtensionAngle = 0
  FormatSpec = %.2w
  FormatSpecOverTolerance = %+.2w
  FormatSpecUnderTolerance = %+.2w
  Inverted = false
  LineAngle = 0
  LockPosition = false
  MeasureType = 1
  OverTolerance = 0
  References2D = -> [View001]
  Rotation = 0
  ScaleType = 0
  ShowUnits = false
  TheoreticalExact = false
  Type = 2
  UnderTolerance = 0
  UseActualArea = true
  X = -1.10807
  Y = -36.25
FEATURE [TechDraw::DrawViewDimension] Dimension036
  AngleOverride = false
  Arbitrary = false
  ArbitraryTolerances = false
  BoxCorners = (2) [(-125,-50,0),(125,50,0)]
  EqualTolerance = true
  ExtensionAngle = 0
  FormatSpec = %.2w
  FormatSpecOverTolerance = %+.2w
  FormatSpecUnderTolerance = %+.2w
  Inverted = false
  LineAngle = 0
  LockPosition = false
  MeasureType = 1
  OverTolerance = 0
  References2D = -> [View001]
  Rotation = 0
  ScaleType = 0
  ShowUnits = false
  TheoreticalExact = false
  Type = 1
  UnderTolerance = 0
  UseActualArea = true
  X = 46.0796
  Y = 15.876
FEATURE [TechDraw::DrawViewDimension] Dimension037
  AngleOverride = false
  Arbitrary = false
  ArbitraryTolerances = false
  BoxCorners = (2) [(-125,-50,0),(125,50,0)]
  EqualTolerance = true
  ExtensionAngle = 0
  FormatSpec = %.2w
  FormatSpecOverTolerance = %+.2w
  FormatSpecUnderTolerance = %+.2w
  Inverted = false
  LineAngle = 0
  LockPosition = false
  MeasureType = 1
  OverTolerance = 0
  References2D = -> [View001]
  Rotation = 0
  ScaleType = 0
  ShowUnits = false
  TheoreticalExact = false
  Type = 1
  UnderTolerance = 0
  UseActualArea = true
  X = -30
  Y = 15.876
FEATURE [TechDraw::DrawViewAnnotation] Annotation016
  Font = osifont
  LineSpace = 100
  LockPosition = false
  MaxWidth = -1
  Owner = -> View001
  Rotation = 0
  ScaleType = 0
  Text = threaded | M4x20
  TextSize = 4
  TextStyle = 0
  X = 0
  Y = 9.24935
FEATURE [TechDraw::DrawPage] Page005  label="Screw holes layout"
  KeepUpdated = true
  NextBalloonIndex = 1
  ProjectionType = 0
  Template = -> Template005
  Views = -> [View001,Dimension,Dimension001,Dimension002,Dimension003,Dimension004,Dimension009,Dimension010,Dimension016,Dimension017,Dimension018,Dimension020,Dimension021,Dimension023,Dimension025,Dimension026,Dimension027,Dimension028,Dimension029,Dimension030,Dimension031,Dimension032,Dimension033,Dimension034,Annotation012,Annotation013,Annotation014,Annotation015,Dimension035,Dimension036,Dimension037,+1 more]
FEATURE [App::DocumentObjectGroup] Group001  label="Drawings"
  Group = -> [Page,Page002,Page003,Page005,Page004]
FEATURE [App::Point] Origin025
  Role = Origin
FEATURE [Sketcher::SketchObject] Sketch034
  ArcFitTolerance = 1e-06
  AttachmentSupport = -> [Origin024]
  ExternalTypes = [0]
  FullyConstrained = true
  MakeInternals = false
  MapMode = 5
  Placement = pos=(0,0,0) rot=(1,0,0;1.5708rad)
  sketch-geometry (8):
    g0: LineSegment StartX=23 StartY=24.3 StartZ=0 EndX=23 EndY=20.8 EndZ=0
    g1: LineSegment StartX=23 StartY=20.8 StartZ=0 EndX=20.5 EndY=20.8 EndZ=0
    g2: LineSegment StartX=20.5 StartY=20.8 StartZ=0 EndX=12 EndY=-9e-16 EndZ=0
    g3: LineSegment StartX=12 StartY=-9e-16 StartZ=0 EndX=0 EndY=-9e-16 EndZ=0
    g4: LineSegment StartX=0 StartY=-9e-16 StartZ=0 EndX=0 EndY=24.3 EndZ=0
    g5: ArcOfCircle CenterX=16.25 CenterY=23.2103 CenterZ=0 NormalX=0 NormalY=0 NormalZ=1 AngleXU=0 Radius=2.5 StartAngle=0.451027 EndAngle=2.69057
    g6: LineSegment StartX=0 StartY=24.3 StartZ=0 EndX=14 EndY=24.3 EndZ=0
    g7: LineSegment StartX=18.5 StartY=24.3 StartZ=0 EndX=23 EndY=24.3 EndZ=0
  constraints (24):
    c: PointOnObject(g4,g-2)
    c: Vertical(g0)
    c: Coincident(g0,g1)
    c: Horizontal(g1)
    c: Coincident(g2,g3)
    c: Horizontal(g3)
    c: Coincident(g3,g4)
    c: Coincident(g3,g-1)
    c: DistanceY(g-1,g4) = 24.3
    c: DistanceX(g4,g0) = 23
    c: Coincident(g6,g4)
    c: Horizontal(g6)
    c: Horizontal(g7,g6)
    c: Horizontal(g7)
    c: Coincident(g0,g7)
    c: DistanceY(g0,g0) = 3.5
    c: Coincident(g2,g1)
    c: DistanceX(g6,g6) = 14
    c: Coincident(g5,g6)
    c: Coincident(g5,g7)
    c: DistanceX(g7,g7) = 4.5
    c: Radius(g5) = 2.5
    c: DistanceX(g1,g1) = 2.5
    c: DistanceX(g3,g3) = 12
FEATURE [PartDesign::Revolution] Revolution002
  Angle = 360
  Angle2 = 0
  Axis = (0,2e-16,1)
  Base = (0,0,0)
  FuseOrder = 0
  Profile = -> Sketch034
  ReferenceAxis = -> Sketch034 [V_Axis]
  Reversed = true
  Suppressed = false
  Type = 0
FEATURE [PartDesign::Body] Body011  label="bmr rough model for fitting"
  AllowCompound = false
  Group = -> [Sketch034,Revolution002]
  Origin = -> Origin024
  Placement = pos=(-45,0,22) rot=(0,0,1;0rad)
  Tip = -> Revolution002
FEATURE [App::Point] Origin027  label="Origin028"
  Role = Origin
FEATURE [Part::Cylinder] Cylinder
  Angle = 360
  AttacherType = Attacher::AttachEngine3D
  FirstAngle = 0
  Height = 12
  Placement = pos=(-45,0,9) rot=(0,0,1;0rad)
  Radius = 12
  SecondAngle = 0
FEATURE [App::Part] Part  label="BMR damping puck"
  Group = -> [Cylinder]
  Origin = -> Origin026
FEATURE [App::DocumentObjectGroup] Group003  label="Separate parts"
  Group = -> [Body003,Body008,Body009,Part]
FEATURE [App::Point] Origin029  label="Origin031"
  Role = Origin
FEATURE [Part::FeaturePython] Tube  # WARN: FeaturePython — macro-defined, semantics opaque (R4)
  AttacherType = Attacher::AttachEngine3D
  Height = 12
  InnerRadius = 12
  OuterRadius = 14
FEATURE [App::Part] Part001  label="damping puck former"
  Group = -> [Tube]
  Origin = -> Origin028
  Placement = pos=(0,300,0) rot=(0,0,1;0rad)
FEATURE [App::DocumentObjectGroup] Group004  label="External models for fitting"
  Group = -> [Body011,Part001,Body005]
